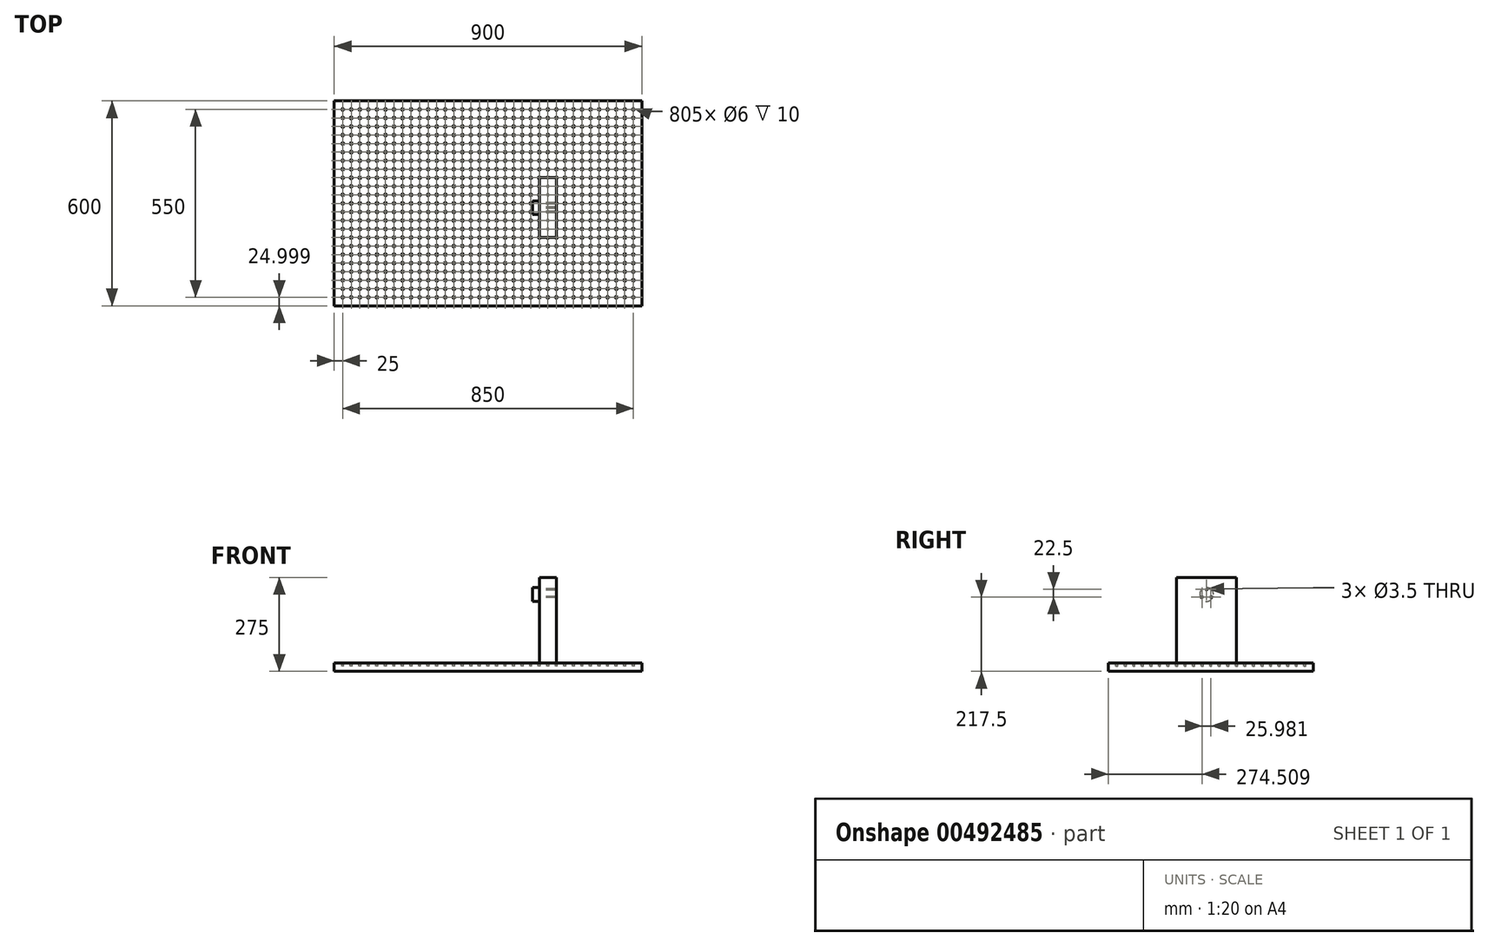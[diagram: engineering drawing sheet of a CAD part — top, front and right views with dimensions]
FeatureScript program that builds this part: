
annotation { "Feature Type Name" : "Feature", "Feature Type Description" : "" }
export const myFeature = defineFeature(function(context is Context, id is Id, definition is map)
    precondition{}
    {
        {
            var Q0;
            Q0=qCreatedBy(makeId("Top.planeOp"),FACE);
            var sketch = newSketch(context, id + "F0", { "sketchPlane" : qUnion([Q0])});
            skLineSegment(sketch, "E0.bottom", {"start": v(0, 7.98) * mm, "end": v(900, 7.98) * mm});
            skLineSegment(sketch, "E0.top", {"start": v(0, 607.98) * mm, "end": v(900, 607.98) * mm});
            skLineSegment(sketch, "E0.left", {"start": v(0, 7.98) * mm, "end": v(0, 607.98) * mm});
            skLineSegment(sketch, "E0.right", {"start": v(900, 7.98) * mm, "end": v(900, 607.98) * mm});
            skSolve(sketch);
        }
        {
            var Q0;
            Q0=makeQuery(id+"F0.imprint","IMPRINT",FACE,{"disambiguationData":[TD([[makeQuery(id+"F0.imprint","IMPRINT",EDGE,{"derivedFrom":sQuery(id+"F0.wireOp",EDGE,"E0.bottom")}),1.0]])]});
            extrude(context, id + "F1", {"entities" : qUnion([Q0]), "depth" : 25 * mm});
        }
        {
            var Q0;
            Q0=makeQuery(id+"F1.opExtrude","CAP_FACE",FACE,{"disambiguationData":[OSD([sQuery(id+"F0.wireOp",EDGE,"E0.bottom"),sQuery(id+"F0.wireOp",EDGE,"E0.top"),sQuery(id+"F0.wireOp",EDGE,"E0.left"),sQuery(id+"F0.wireOp",EDGE,"E0.right")])],"isStart":false});
            var sketch = newSketch(context, id + "F2", { "sketchPlane" : qUnion([Q0])});
            skCircle(sketch, "E1", {"center": v(25, 32.98) * mm, "radius": 3 * mm});
            skCircle(sketch, "E2.0.1.0", {"center": v(25, 57.98) * mm, "radius": 3 * mm});
            skCircle(sketch, "E2.0.2.0", {"center": v(25, 82.98) * mm, "radius": 3 * mm});
            skCircle(sketch, "E2.0.3.0", {"center": v(25, 107.98) * mm, "radius": 3 * mm});
            skCircle(sketch, "E2.0.4.0", {"center": v(25, 132.98) * mm, "radius": 3 * mm});
            skCircle(sketch, "E2.0.5.0", {"center": v(25, 157.98) * mm, "radius": 3 * mm});
            skCircle(sketch, "E2.0.6.0", {"center": v(25, 182.98) * mm, "radius": 3 * mm});
            skCircle(sketch, "E2.0.7.0", {"center": v(25, 207.98) * mm, "radius": 3 * mm});
            skCircle(sketch, "E2.0.8.0", {"center": v(25, 232.98) * mm, "radius": 3 * mm});
            skCircle(sketch, "E2.0.9.0", {"center": v(25, 257.98) * mm, "radius": 3 * mm});
            skCircle(sketch, "E2.0.10.0", {"center": v(25, 282.98) * mm, "radius": 3 * mm});
            skCircle(sketch, "E2.0.11.0", {"center": v(25, 307.98) * mm, "radius": 3 * mm});
            skCircle(sketch, "E2.0.12.0", {"center": v(25, 332.98) * mm, "radius": 3 * mm});
            skCircle(sketch, "E2.0.13.0", {"center": v(25, 357.98) * mm, "radius": 3 * mm});
            skCircle(sketch, "E2.0.14.0", {"center": v(25, 382.98) * mm, "radius": 3 * mm});
            skCircle(sketch, "E2.0.15.0", {"center": v(25, 407.98) * mm, "radius": 3 * mm});
            skCircle(sketch, "E2.0.16.0", {"center": v(25, 432.98) * mm, "radius": 3 * mm});
            skCircle(sketch, "E2.0.17.0", {"center": v(25, 457.98) * mm, "radius": 3 * mm});
            skCircle(sketch, "E2.0.18.0", {"center": v(25, 482.98) * mm, "radius": 3 * mm});
            skCircle(sketch, "E2.0.19.0", {"center": v(25, 507.98) * mm, "radius": 3 * mm});
            skCircle(sketch, "E2.0.20.0", {"center": v(25, 532.98) * mm, "radius": 3 * mm});
            skCircle(sketch, "E2.0.21.0", {"center": v(25, 557.98) * mm, "radius": 3 * mm});
            skCircle(sketch, "E2.0.22.0", {"center": v(25, 582.98) * mm, "radius": 3 * mm});
            skCircle(sketch, "E2.1.0.0", {"center": v(50, 32.98) * mm, "radius": 3 * mm});
            skCircle(sketch, "E2.1.1.0", {"center": v(50, 57.98) * mm, "radius": 3 * mm});
            skCircle(sketch, "E2.1.2.0", {"center": v(50, 82.98) * mm, "radius": 3 * mm});
            skCircle(sketch, "E2.1.3.0", {"center": v(50, 107.98) * mm, "radius": 3 * mm});
            skCircle(sketch, "E2.1.4.0", {"center": v(50, 132.98) * mm, "radius": 3 * mm});
            skCircle(sketch, "E2.1.5.0", {"center": v(50, 157.98) * mm, "radius": 3 * mm});
            skCircle(sketch, "E2.1.6.0", {"center": v(50, 182.98) * mm, "radius": 3 * mm});
            skCircle(sketch, "E2.1.7.0", {"center": v(50, 207.98) * mm, "radius": 3 * mm});
            skCircle(sketch, "E2.1.8.0", {"center": v(50, 232.98) * mm, "radius": 3 * mm});
            skCircle(sketch, "E2.1.9.0", {"center": v(50, 257.98) * mm, "radius": 3 * mm});
            skCircle(sketch, "E2.1.10.0", {"center": v(50, 282.98) * mm, "radius": 3 * mm});
            skCircle(sketch, "E2.1.11.0", {"center": v(50, 307.98) * mm, "radius": 3 * mm});
            skCircle(sketch, "E2.1.12.0", {"center": v(50, 332.98) * mm, "radius": 3 * mm});
            skCircle(sketch, "E2.1.13.0", {"center": v(50, 357.98) * mm, "radius": 3 * mm});
            skCircle(sketch, "E2.1.14.0", {"center": v(50, 382.98) * mm, "radius": 3 * mm});
            skCircle(sketch, "E2.1.15.0", {"center": v(50, 407.98) * mm, "radius": 3 * mm});
            skCircle(sketch, "E2.1.16.0", {"center": v(50, 432.98) * mm, "radius": 3 * mm});
            skCircle(sketch, "E2.1.17.0", {"center": v(50, 457.98) * mm, "radius": 3 * mm});
            skCircle(sketch, "E2.1.18.0", {"center": v(50, 482.98) * mm, "radius": 3 * mm});
            skCircle(sketch, "E2.1.19.0", {"center": v(50, 507.98) * mm, "radius": 3 * mm});
            skCircle(sketch, "E2.1.20.0", {"center": v(50, 532.98) * mm, "radius": 3 * mm});
            skCircle(sketch, "E2.1.21.0", {"center": v(50, 557.98) * mm, "radius": 3 * mm});
            skCircle(sketch, "E2.1.22.0", {"center": v(50, 582.98) * mm, "radius": 3 * mm});
            skCircle(sketch, "E2.2.0.0", {"center": v(75, 32.98) * mm, "radius": 3 * mm});
            skCircle(sketch, "E2.2.1.0", {"center": v(75, 57.98) * mm, "radius": 3 * mm});
            skCircle(sketch, "E2.2.2.0", {"center": v(75, 82.98) * mm, "radius": 3 * mm});
            skCircle(sketch, "E2.2.3.0", {"center": v(75, 107.98) * mm, "radius": 3 * mm});
            skCircle(sketch, "E2.2.4.0", {"center": v(75, 132.98) * mm, "radius": 3 * mm});
            skCircle(sketch, "E2.2.5.0", {"center": v(75, 157.98) * mm, "radius": 3 * mm});
            skCircle(sketch, "E2.2.6.0", {"center": v(75, 182.98) * mm, "radius": 3 * mm});
            skCircle(sketch, "E2.2.7.0", {"center": v(75, 207.98) * mm, "radius": 3 * mm});
            skCircle(sketch, "E2.2.8.0", {"center": v(75, 232.98) * mm, "radius": 3 * mm});
            skCircle(sketch, "E2.2.9.0", {"center": v(75, 257.98) * mm, "radius": 3 * mm});
            skCircle(sketch, "E2.2.10.0", {"center": v(75, 282.98) * mm, "radius": 3 * mm});
            skCircle(sketch, "E2.2.11.0", {"center": v(75, 307.98) * mm, "radius": 3 * mm});
            skCircle(sketch, "E2.2.12.0", {"center": v(75, 332.98) * mm, "radius": 3 * mm});
            skCircle(sketch, "E2.2.13.0", {"center": v(75, 357.98) * mm, "radius": 3 * mm});
            skCircle(sketch, "E2.2.14.0", {"center": v(75, 382.98) * mm, "radius": 3 * mm});
            skCircle(sketch, "E2.2.15.0", {"center": v(75, 407.98) * mm, "radius": 3 * mm});
            skCircle(sketch, "E2.2.16.0", {"center": v(75, 432.98) * mm, "radius": 3 * mm});
            skCircle(sketch, "E2.2.17.0", {"center": v(75, 457.98) * mm, "radius": 3 * mm});
            skCircle(sketch, "E2.2.18.0", {"center": v(75, 482.98) * mm, "radius": 3 * mm});
            skCircle(sketch, "E2.2.19.0", {"center": v(75, 507.98) * mm, "radius": 3 * mm});
            skCircle(sketch, "E2.2.20.0", {"center": v(75, 532.98) * mm, "radius": 3 * mm});
            skCircle(sketch, "E2.2.21.0", {"center": v(75, 557.98) * mm, "radius": 3 * mm});
            skCircle(sketch, "E2.2.22.0", {"center": v(75, 582.98) * mm, "radius": 3 * mm});
            skCircle(sketch, "E2.3.0.0", {"center": v(100, 32.98) * mm, "radius": 3 * mm});
            skCircle(sketch, "E2.3.1.0", {"center": v(100, 57.98) * mm, "radius": 3 * mm});
            skCircle(sketch, "E2.3.2.0", {"center": v(100, 82.98) * mm, "radius": 3 * mm});
            skCircle(sketch, "E2.3.3.0", {"center": v(100, 107.98) * mm, "radius": 3 * mm});
            skCircle(sketch, "E2.3.4.0", {"center": v(100, 132.98) * mm, "radius": 3 * mm});
            skCircle(sketch, "E2.3.5.0", {"center": v(100, 157.98) * mm, "radius": 3 * mm});
            skCircle(sketch, "E2.3.6.0", {"center": v(100, 182.98) * mm, "radius": 3 * mm});
            skCircle(sketch, "E2.3.7.0", {"center": v(100, 207.98) * mm, "radius": 3 * mm});
            skCircle(sketch, "E2.3.8.0", {"center": v(100, 232.98) * mm, "radius": 3 * mm});
            skCircle(sketch, "E2.3.9.0", {"center": v(100, 257.98) * mm, "radius": 3 * mm});
            skCircle(sketch, "E2.3.10.0", {"center": v(100, 282.98) * mm, "radius": 3 * mm});
            skCircle(sketch, "E2.3.11.0", {"center": v(100, 307.98) * mm, "radius": 3 * mm});
            skCircle(sketch, "E2.3.12.0", {"center": v(100, 332.98) * mm, "radius": 3 * mm});
            skCircle(sketch, "E2.3.13.0", {"center": v(100, 357.98) * mm, "radius": 3 * mm});
            skCircle(sketch, "E2.3.14.0", {"center": v(100, 382.98) * mm, "radius": 3 * mm});
            skCircle(sketch, "E2.3.15.0", {"center": v(100, 407.98) * mm, "radius": 3 * mm});
            skCircle(sketch, "E2.3.16.0", {"center": v(100, 432.98) * mm, "radius": 3 * mm});
            skCircle(sketch, "E2.3.17.0", {"center": v(100, 457.98) * mm, "radius": 3 * mm});
            skCircle(sketch, "E2.3.18.0", {"center": v(100, 482.98) * mm, "radius": 3 * mm});
            skCircle(sketch, "E2.3.19.0", {"center": v(100, 507.98) * mm, "radius": 3 * mm});
            skCircle(sketch, "E2.3.20.0", {"center": v(100, 532.98) * mm, "radius": 3 * mm});
            skCircle(sketch, "E2.3.21.0", {"center": v(100, 557.98) * mm, "radius": 3 * mm});
            skCircle(sketch, "E2.3.22.0", {"center": v(100, 582.98) * mm, "radius": 3 * mm});
            skCircle(sketch, "E2.4.0.0", {"center": v(125, 32.98) * mm, "radius": 3 * mm});
            skCircle(sketch, "E2.4.1.0", {"center": v(125, 57.98) * mm, "radius": 3 * mm});
            skCircle(sketch, "E2.4.2.0", {"center": v(125, 82.98) * mm, "radius": 3 * mm});
            skCircle(sketch, "E2.4.3.0", {"center": v(125, 107.98) * mm, "radius": 3 * mm});
            skCircle(sketch, "E2.4.4.0", {"center": v(125, 132.98) * mm, "radius": 3 * mm});
            skCircle(sketch, "E2.4.5.0", {"center": v(125, 157.98) * mm, "radius": 3 * mm});
            skCircle(sketch, "E2.4.6.0", {"center": v(125, 182.98) * mm, "radius": 3 * mm});
            skCircle(sketch, "E2.4.7.0", {"center": v(125, 207.98) * mm, "radius": 3 * mm});
            skCircle(sketch, "E2.4.8.0", {"center": v(125, 232.98) * mm, "radius": 3 * mm});
            skCircle(sketch, "E2.4.9.0", {"center": v(125, 257.98) * mm, "radius": 3 * mm});
            skCircle(sketch, "E2.4.10.0", {"center": v(125, 282.98) * mm, "radius": 3 * mm});
            skCircle(sketch, "E2.4.11.0", {"center": v(125, 307.98) * mm, "radius": 3 * mm});
            skCircle(sketch, "E2.4.12.0", {"center": v(125, 332.98) * mm, "radius": 3 * mm});
            skCircle(sketch, "E2.4.13.0", {"center": v(125, 357.98) * mm, "radius": 3 * mm});
            skCircle(sketch, "E2.4.14.0", {"center": v(125, 382.98) * mm, "radius": 3 * mm});
            skCircle(sketch, "E2.4.15.0", {"center": v(125, 407.98) * mm, "radius": 3 * mm});
            skCircle(sketch, "E2.4.16.0", {"center": v(125, 432.98) * mm, "radius": 3 * mm});
            skCircle(sketch, "E2.4.17.0", {"center": v(125, 457.98) * mm, "radius": 3 * mm});
            skCircle(sketch, "E2.4.18.0", {"center": v(125, 482.98) * mm, "radius": 3 * mm});
            skCircle(sketch, "E2.4.19.0", {"center": v(125, 507.98) * mm, "radius": 3 * mm});
            skCircle(sketch, "E2.4.20.0", {"center": v(125, 532.98) * mm, "radius": 3 * mm});
            skCircle(sketch, "E2.4.21.0", {"center": v(125, 557.98) * mm, "radius": 3 * mm});
            skCircle(sketch, "E2.4.22.0", {"center": v(125, 582.98) * mm, "radius": 3 * mm});
            skCircle(sketch, "E2.5.0.0", {"center": v(150, 32.98) * mm, "radius": 3 * mm});
            skCircle(sketch, "E2.5.1.0", {"center": v(150, 57.98) * mm, "radius": 3 * mm});
            skCircle(sketch, "E2.5.2.0", {"center": v(150, 82.98) * mm, "radius": 3 * mm});
            skCircle(sketch, "E2.5.3.0", {"center": v(150, 107.98) * mm, "radius": 3 * mm});
            skCircle(sketch, "E2.5.4.0", {"center": v(150, 132.98) * mm, "radius": 3 * mm});
            skCircle(sketch, "E2.5.5.0", {"center": v(150, 157.98) * mm, "radius": 3 * mm});
            skCircle(sketch, "E2.5.6.0", {"center": v(150, 182.98) * mm, "radius": 3 * mm});
            skCircle(sketch, "E2.5.7.0", {"center": v(150, 207.98) * mm, "radius": 3 * mm});
            skCircle(sketch, "E2.5.8.0", {"center": v(150, 232.98) * mm, "radius": 3 * mm});
            skCircle(sketch, "E2.5.9.0", {"center": v(150, 257.98) * mm, "radius": 3 * mm});
            skCircle(sketch, "E2.5.10.0", {"center": v(150, 282.98) * mm, "radius": 3 * mm});
            skCircle(sketch, "E2.5.11.0", {"center": v(150, 307.98) * mm, "radius": 3 * mm});
            skCircle(sketch, "E2.5.12.0", {"center": v(150, 332.98) * mm, "radius": 3 * mm});
            skCircle(sketch, "E2.5.13.0", {"center": v(150, 357.98) * mm, "radius": 3 * mm});
            skCircle(sketch, "E2.5.14.0", {"center": v(150, 382.98) * mm, "radius": 3 * mm});
            skCircle(sketch, "E2.5.15.0", {"center": v(150, 407.98) * mm, "radius": 3 * mm});
            skCircle(sketch, "E2.5.16.0", {"center": v(150, 432.98) * mm, "radius": 3 * mm});
            skCircle(sketch, "E2.5.17.0", {"center": v(150, 457.98) * mm, "radius": 3 * mm});
            skCircle(sketch, "E2.5.18.0", {"center": v(150, 482.98) * mm, "radius": 3 * mm});
            skCircle(sketch, "E2.5.19.0", {"center": v(150, 507.98) * mm, "radius": 3 * mm});
            skCircle(sketch, "E2.5.20.0", {"center": v(150, 532.98) * mm, "radius": 3 * mm});
            skCircle(sketch, "E2.5.21.0", {"center": v(150, 557.98) * mm, "radius": 3 * mm});
            skCircle(sketch, "E2.5.22.0", {"center": v(150, 582.98) * mm, "radius": 3 * mm});
            skCircle(sketch, "E2.6.0.0", {"center": v(175, 32.98) * mm, "radius": 3 * mm});
            skCircle(sketch, "E2.6.1.0", {"center": v(175, 57.98) * mm, "radius": 3 * mm});
            skCircle(sketch, "E2.6.2.0", {"center": v(175, 82.98) * mm, "radius": 3 * mm});
            skCircle(sketch, "E2.6.3.0", {"center": v(175, 107.98) * mm, "radius": 3 * mm});
            skCircle(sketch, "E2.6.4.0", {"center": v(175, 132.98) * mm, "radius": 3 * mm});
            skCircle(sketch, "E2.6.5.0", {"center": v(175, 157.98) * mm, "radius": 3 * mm});
            skCircle(sketch, "E2.6.6.0", {"center": v(175, 182.98) * mm, "radius": 3 * mm});
            skCircle(sketch, "E2.6.7.0", {"center": v(175, 207.98) * mm, "radius": 3 * mm});
            skCircle(sketch, "E2.6.8.0", {"center": v(175, 232.98) * mm, "radius": 3 * mm});
            skCircle(sketch, "E2.6.9.0", {"center": v(175, 257.98) * mm, "radius": 3 * mm});
            skCircle(sketch, "E2.6.10.0", {"center": v(175, 282.98) * mm, "radius": 3 * mm});
            skCircle(sketch, "E2.6.11.0", {"center": v(175, 307.98) * mm, "radius": 3 * mm});
            skCircle(sketch, "E2.6.12.0", {"center": v(175, 332.98) * mm, "radius": 3 * mm});
            skCircle(sketch, "E2.6.13.0", {"center": v(175, 357.98) * mm, "radius": 3 * mm});
            skCircle(sketch, "E2.6.14.0", {"center": v(175, 382.98) * mm, "radius": 3 * mm});
            skCircle(sketch, "E2.6.15.0", {"center": v(175, 407.98) * mm, "radius": 3 * mm});
            skCircle(sketch, "E2.6.16.0", {"center": v(175, 432.98) * mm, "radius": 3 * mm});
            skCircle(sketch, "E2.6.17.0", {"center": v(175, 457.98) * mm, "radius": 3 * mm});
            skCircle(sketch, "E2.6.18.0", {"center": v(175, 482.98) * mm, "radius": 3 * mm});
            skCircle(sketch, "E2.6.19.0", {"center": v(175, 507.98) * mm, "radius": 3 * mm});
            skCircle(sketch, "E2.6.20.0", {"center": v(175, 532.98) * mm, "radius": 3 * mm});
            skCircle(sketch, "E2.6.21.0", {"center": v(175, 557.98) * mm, "radius": 3 * mm});
            skCircle(sketch, "E2.6.22.0", {"center": v(175, 582.98) * mm, "radius": 3 * mm});
            skCircle(sketch, "E2.7.0.0", {"center": v(200, 32.98) * mm, "radius": 3 * mm});
            skCircle(sketch, "E2.7.1.0", {"center": v(200, 57.98) * mm, "radius": 3 * mm});
            skCircle(sketch, "E2.7.2.0", {"center": v(200, 82.98) * mm, "radius": 3 * mm});
            skCircle(sketch, "E2.7.3.0", {"center": v(200, 107.98) * mm, "radius": 3 * mm});
            skCircle(sketch, "E2.7.4.0", {"center": v(200, 132.98) * mm, "radius": 3 * mm});
            skCircle(sketch, "E2.7.5.0", {"center": v(200, 157.98) * mm, "radius": 3 * mm});
            skCircle(sketch, "E2.7.6.0", {"center": v(200, 182.98) * mm, "radius": 3 * mm});
            skCircle(sketch, "E2.7.7.0", {"center": v(200, 207.98) * mm, "radius": 3 * mm});
            skCircle(sketch, "E2.7.8.0", {"center": v(200, 232.98) * mm, "radius": 3 * mm});
            skCircle(sketch, "E2.7.9.0", {"center": v(200, 257.98) * mm, "radius": 3 * mm});
            skCircle(sketch, "E2.7.10.0", {"center": v(200, 282.98) * mm, "radius": 3 * mm});
            skCircle(sketch, "E2.7.11.0", {"center": v(200, 307.98) * mm, "radius": 3 * mm});
            skCircle(sketch, "E2.7.12.0", {"center": v(200, 332.98) * mm, "radius": 3 * mm});
            skCircle(sketch, "E2.7.13.0", {"center": v(200, 357.98) * mm, "radius": 3 * mm});
            skCircle(sketch, "E2.7.14.0", {"center": v(200, 382.98) * mm, "radius": 3 * mm});
            skCircle(sketch, "E2.7.15.0", {"center": v(200, 407.98) * mm, "radius": 3 * mm});
            skCircle(sketch, "E2.7.16.0", {"center": v(200, 432.98) * mm, "radius": 3 * mm});
            skCircle(sketch, "E2.7.17.0", {"center": v(200, 457.98) * mm, "radius": 3 * mm});
            skCircle(sketch, "E2.7.18.0", {"center": v(200, 482.98) * mm, "radius": 3 * mm});
            skCircle(sketch, "E2.7.19.0", {"center": v(200, 507.98) * mm, "radius": 3 * mm});
            skCircle(sketch, "E2.7.20.0", {"center": v(200, 532.98) * mm, "radius": 3 * mm});
            skCircle(sketch, "E2.7.21.0", {"center": v(200, 557.98) * mm, "radius": 3 * mm});
            skCircle(sketch, "E2.7.22.0", {"center": v(200, 582.98) * mm, "radius": 3 * mm});
            skCircle(sketch, "E2.8.0.0", {"center": v(225, 32.98) * mm, "radius": 3 * mm});
            skCircle(sketch, "E2.8.1.0", {"center": v(225, 57.98) * mm, "radius": 3 * mm});
            skCircle(sketch, "E2.8.2.0", {"center": v(225, 82.98) * mm, "radius": 3 * mm});
            skCircle(sketch, "E2.8.3.0", {"center": v(225, 107.98) * mm, "radius": 3 * mm});
            skCircle(sketch, "E2.8.4.0", {"center": v(225, 132.98) * mm, "radius": 3 * mm});
            skCircle(sketch, "E2.8.5.0", {"center": v(225, 157.98) * mm, "radius": 3 * mm});
            skCircle(sketch, "E2.8.6.0", {"center": v(225, 182.98) * mm, "radius": 3 * mm});
            skCircle(sketch, "E2.8.7.0", {"center": v(225, 207.98) * mm, "radius": 3 * mm});
            skCircle(sketch, "E2.8.8.0", {"center": v(225, 232.98) * mm, "radius": 3 * mm});
            skCircle(sketch, "E2.8.9.0", {"center": v(225, 257.98) * mm, "radius": 3 * mm});
            skCircle(sketch, "E2.8.10.0", {"center": v(225, 282.98) * mm, "radius": 3 * mm});
            skCircle(sketch, "E2.8.11.0", {"center": v(225, 307.98) * mm, "radius": 3 * mm});
            skCircle(sketch, "E2.8.12.0", {"center": v(225, 332.98) * mm, "radius": 3 * mm});
            skCircle(sketch, "E2.8.13.0", {"center": v(225, 357.98) * mm, "radius": 3 * mm});
            skCircle(sketch, "E2.8.14.0", {"center": v(225, 382.98) * mm, "radius": 3 * mm});
            skCircle(sketch, "E2.8.15.0", {"center": v(225, 407.98) * mm, "radius": 3 * mm});
            skCircle(sketch, "E2.8.16.0", {"center": v(225, 432.98) * mm, "radius": 3 * mm});
            skCircle(sketch, "E2.8.17.0", {"center": v(225, 457.98) * mm, "radius": 3 * mm});
            skCircle(sketch, "E2.8.18.0", {"center": v(225, 482.98) * mm, "radius": 3 * mm});
            skCircle(sketch, "E2.8.19.0", {"center": v(225, 507.98) * mm, "radius": 3 * mm});
            skCircle(sketch, "E2.8.20.0", {"center": v(225, 532.98) * mm, "radius": 3 * mm});
            skCircle(sketch, "E2.8.21.0", {"center": v(225, 557.98) * mm, "radius": 3 * mm});
            skCircle(sketch, "E2.8.22.0", {"center": v(225, 582.98) * mm, "radius": 3 * mm});
            skCircle(sketch, "E2.9.0.0", {"center": v(250, 32.98) * mm, "radius": 3 * mm});
            skCircle(sketch, "E2.9.1.0", {"center": v(250, 57.98) * mm, "radius": 3 * mm});
            skCircle(sketch, "E2.9.2.0", {"center": v(250, 82.98) * mm, "radius": 3 * mm});
            skCircle(sketch, "E2.9.3.0", {"center": v(250, 107.98) * mm, "radius": 3 * mm});
            skCircle(sketch, "E2.9.4.0", {"center": v(250, 132.98) * mm, "radius": 3 * mm});
            skCircle(sketch, "E2.9.5.0", {"center": v(250, 157.98) * mm, "radius": 3 * mm});
            skCircle(sketch, "E2.9.6.0", {"center": v(250, 182.98) * mm, "radius": 3 * mm});
            skCircle(sketch, "E2.9.7.0", {"center": v(250, 207.98) * mm, "radius": 3 * mm});
            skCircle(sketch, "E2.9.8.0", {"center": v(250, 232.98) * mm, "radius": 3 * mm});
            skCircle(sketch, "E2.9.9.0", {"center": v(250, 257.98) * mm, "radius": 3 * mm});
            skCircle(sketch, "E2.9.10.0", {"center": v(250, 282.98) * mm, "radius": 3 * mm});
            skCircle(sketch, "E2.9.11.0", {"center": v(250, 307.98) * mm, "radius": 3 * mm});
            skCircle(sketch, "E2.9.12.0", {"center": v(250, 332.98) * mm, "radius": 3 * mm});
            skCircle(sketch, "E2.9.13.0", {"center": v(250, 357.98) * mm, "radius": 3 * mm});
            skCircle(sketch, "E2.9.14.0", {"center": v(250, 382.98) * mm, "radius": 3 * mm});
            skCircle(sketch, "E2.9.15.0", {"center": v(250, 407.98) * mm, "radius": 3 * mm});
            skCircle(sketch, "E2.9.16.0", {"center": v(250, 432.98) * mm, "radius": 3 * mm});
            skCircle(sketch, "E2.9.17.0", {"center": v(250, 457.98) * mm, "radius": 3 * mm});
            skCircle(sketch, "E2.9.18.0", {"center": v(250, 482.98) * mm, "radius": 3 * mm});
            skCircle(sketch, "E2.9.19.0", {"center": v(250, 507.98) * mm, "radius": 3 * mm});
            skCircle(sketch, "E2.9.20.0", {"center": v(250, 532.98) * mm, "radius": 3 * mm});
            skCircle(sketch, "E2.9.21.0", {"center": v(250, 557.98) * mm, "radius": 3 * mm});
            skCircle(sketch, "E2.9.22.0", {"center": v(250, 582.98) * mm, "radius": 3 * mm});
            skCircle(sketch, "E2.10.0.0", {"center": v(275, 32.98) * mm, "radius": 3 * mm});
            skCircle(sketch, "E2.10.1.0", {"center": v(275, 57.98) * mm, "radius": 3 * mm});
            skCircle(sketch, "E2.10.2.0", {"center": v(275, 82.98) * mm, "radius": 3 * mm});
            skCircle(sketch, "E2.10.3.0", {"center": v(275, 107.98) * mm, "radius": 3 * mm});
            skCircle(sketch, "E2.10.4.0", {"center": v(275, 132.98) * mm, "radius": 3 * mm});
            skCircle(sketch, "E2.10.5.0", {"center": v(275, 157.98) * mm, "radius": 3 * mm});
            skCircle(sketch, "E2.10.6.0", {"center": v(275, 182.98) * mm, "radius": 3 * mm});
            skCircle(sketch, "E2.10.7.0", {"center": v(275, 207.98) * mm, "radius": 3 * mm});
            skCircle(sketch, "E2.10.8.0", {"center": v(275, 232.98) * mm, "radius": 3 * mm});
            skCircle(sketch, "E2.10.9.0", {"center": v(275, 257.98) * mm, "radius": 3 * mm});
            skCircle(sketch, "E2.10.10.0", {"center": v(275, 282.98) * mm, "radius": 3 * mm});
            skCircle(sketch, "E2.10.11.0", {"center": v(275, 307.98) * mm, "radius": 3 * mm});
            skCircle(sketch, "E2.10.12.0", {"center": v(275, 332.98) * mm, "radius": 3 * mm});
            skCircle(sketch, "E2.10.13.0", {"center": v(275, 357.98) * mm, "radius": 3 * mm});
            skCircle(sketch, "E2.10.14.0", {"center": v(275, 382.98) * mm, "radius": 3 * mm});
            skCircle(sketch, "E2.10.15.0", {"center": v(275, 407.98) * mm, "radius": 3 * mm});
            skCircle(sketch, "E2.10.16.0", {"center": v(275, 432.98) * mm, "radius": 3 * mm});
            skCircle(sketch, "E2.10.17.0", {"center": v(275, 457.98) * mm, "radius": 3 * mm});
            skCircle(sketch, "E2.10.18.0", {"center": v(275, 482.98) * mm, "radius": 3 * mm});
            skCircle(sketch, "E2.10.19.0", {"center": v(275, 507.98) * mm, "radius": 3 * mm});
            skCircle(sketch, "E2.10.20.0", {"center": v(275, 532.98) * mm, "radius": 3 * mm});
            skCircle(sketch, "E2.10.21.0", {"center": v(275, 557.98) * mm, "radius": 3 * mm});
            skCircle(sketch, "E2.10.22.0", {"center": v(275, 582.98) * mm, "radius": 3 * mm});
            skCircle(sketch, "E2.11.0.0", {"center": v(300, 32.98) * mm, "radius": 3 * mm});
            skCircle(sketch, "E2.11.1.0", {"center": v(300, 57.98) * mm, "radius": 3 * mm});
            skCircle(sketch, "E2.11.2.0", {"center": v(300, 82.98) * mm, "radius": 3 * mm});
            skCircle(sketch, "E2.11.3.0", {"center": v(300, 107.98) * mm, "radius": 3 * mm});
            skCircle(sketch, "E2.11.4.0", {"center": v(300, 132.98) * mm, "radius": 3 * mm});
            skCircle(sketch, "E2.11.5.0", {"center": v(300, 157.98) * mm, "radius": 3 * mm});
            skCircle(sketch, "E2.11.6.0", {"center": v(300, 182.98) * mm, "radius": 3 * mm});
            skCircle(sketch, "E2.11.7.0", {"center": v(300, 207.98) * mm, "radius": 3 * mm});
            skCircle(sketch, "E2.11.8.0", {"center": v(300, 232.98) * mm, "radius": 3 * mm});
            skCircle(sketch, "E2.11.9.0", {"center": v(300, 257.98) * mm, "radius": 3 * mm});
            skCircle(sketch, "E2.11.10.0", {"center": v(300, 282.98) * mm, "radius": 3 * mm});
            skCircle(sketch, "E2.11.11.0", {"center": v(300, 307.98) * mm, "radius": 3 * mm});
            skCircle(sketch, "E2.11.12.0", {"center": v(300, 332.98) * mm, "radius": 3 * mm});
            skCircle(sketch, "E2.11.13.0", {"center": v(300, 357.98) * mm, "radius": 3 * mm});
            skCircle(sketch, "E2.11.14.0", {"center": v(300, 382.98) * mm, "radius": 3 * mm});
            skCircle(sketch, "E2.11.15.0", {"center": v(300, 407.98) * mm, "radius": 3 * mm});
            skCircle(sketch, "E2.11.16.0", {"center": v(300, 432.98) * mm, "radius": 3 * mm});
            skCircle(sketch, "E2.11.17.0", {"center": v(300, 457.98) * mm, "radius": 3 * mm});
            skCircle(sketch, "E2.11.18.0", {"center": v(300, 482.98) * mm, "radius": 3 * mm});
            skCircle(sketch, "E2.11.19.0", {"center": v(300, 507.98) * mm, "radius": 3 * mm});
            skCircle(sketch, "E2.11.20.0", {"center": v(300, 532.98) * mm, "radius": 3 * mm});
            skCircle(sketch, "E2.11.21.0", {"center": v(300, 557.98) * mm, "radius": 3 * mm});
            skCircle(sketch, "E2.11.22.0", {"center": v(300, 582.98) * mm, "radius": 3 * mm});
            skCircle(sketch, "E2.12.0.0", {"center": v(325, 32.98) * mm, "radius": 3 * mm});
            skCircle(sketch, "E2.12.1.0", {"center": v(325, 57.98) * mm, "radius": 3 * mm});
            skCircle(sketch, "E2.12.2.0", {"center": v(325, 82.98) * mm, "radius": 3 * mm});
            skCircle(sketch, "E2.12.3.0", {"center": v(325, 107.98) * mm, "radius": 3 * mm});
            skCircle(sketch, "E2.12.4.0", {"center": v(325, 132.98) * mm, "radius": 3 * mm});
            skCircle(sketch, "E2.12.5.0", {"center": v(325, 157.98) * mm, "radius": 3 * mm});
            skCircle(sketch, "E2.12.6.0", {"center": v(325, 182.98) * mm, "radius": 3 * mm});
            skCircle(sketch, "E2.12.7.0", {"center": v(325, 207.98) * mm, "radius": 3 * mm});
            skCircle(sketch, "E2.12.8.0", {"center": v(325, 232.98) * mm, "radius": 3 * mm});
            skCircle(sketch, "E2.12.9.0", {"center": v(325, 257.98) * mm, "radius": 3 * mm});
            skCircle(sketch, "E2.12.10.0", {"center": v(325, 282.98) * mm, "radius": 3 * mm});
            skCircle(sketch, "E2.12.11.0", {"center": v(325, 307.98) * mm, "radius": 3 * mm});
            skCircle(sketch, "E2.12.12.0", {"center": v(325, 332.98) * mm, "radius": 3 * mm});
            skCircle(sketch, "E2.12.13.0", {"center": v(325, 357.98) * mm, "radius": 3 * mm});
            skCircle(sketch, "E2.12.14.0", {"center": v(325, 382.98) * mm, "radius": 3 * mm});
            skCircle(sketch, "E2.12.15.0", {"center": v(325, 407.98) * mm, "radius": 3 * mm});
            skCircle(sketch, "E2.12.16.0", {"center": v(325, 432.98) * mm, "radius": 3 * mm});
            skCircle(sketch, "E2.12.17.0", {"center": v(325, 457.98) * mm, "radius": 3 * mm});
            skCircle(sketch, "E2.12.18.0", {"center": v(325, 482.98) * mm, "radius": 3 * mm});
            skCircle(sketch, "E2.12.19.0", {"center": v(325, 507.98) * mm, "radius": 3 * mm});
            skCircle(sketch, "E2.12.20.0", {"center": v(325, 532.98) * mm, "radius": 3 * mm});
            skCircle(sketch, "E2.12.21.0", {"center": v(325, 557.98) * mm, "radius": 3 * mm});
            skCircle(sketch, "E2.12.22.0", {"center": v(325, 582.98) * mm, "radius": 3 * mm});
            skCircle(sketch, "E2.13.0.0", {"center": v(350, 32.98) * mm, "radius": 3 * mm});
            skCircle(sketch, "E2.13.1.0", {"center": v(350, 57.98) * mm, "radius": 3 * mm});
            skCircle(sketch, "E2.13.2.0", {"center": v(350, 82.98) * mm, "radius": 3 * mm});
            skCircle(sketch, "E2.13.3.0", {"center": v(350, 107.98) * mm, "radius": 3 * mm});
            skCircle(sketch, "E2.13.4.0", {"center": v(350, 132.98) * mm, "radius": 3 * mm});
            skCircle(sketch, "E2.13.5.0", {"center": v(350, 157.98) * mm, "radius": 3 * mm});
            skCircle(sketch, "E2.13.6.0", {"center": v(350, 182.98) * mm, "radius": 3 * mm});
            skCircle(sketch, "E2.13.7.0", {"center": v(350, 207.98) * mm, "radius": 3 * mm});
            skCircle(sketch, "E2.13.8.0", {"center": v(350, 232.98) * mm, "radius": 3 * mm});
            skCircle(sketch, "E2.13.9.0", {"center": v(350, 257.98) * mm, "radius": 3 * mm});
            skCircle(sketch, "E2.13.10.0", {"center": v(350, 282.98) * mm, "radius": 3 * mm});
            skCircle(sketch, "E2.13.11.0", {"center": v(350, 307.98) * mm, "radius": 3 * mm});
            skCircle(sketch, "E2.13.12.0", {"center": v(350, 332.98) * mm, "radius": 3 * mm});
            skCircle(sketch, "E2.13.13.0", {"center": v(350, 357.98) * mm, "radius": 3 * mm});
            skCircle(sketch, "E2.13.14.0", {"center": v(350, 382.98) * mm, "radius": 3 * mm});
            skCircle(sketch, "E2.13.15.0", {"center": v(350, 407.98) * mm, "radius": 3 * mm});
            skCircle(sketch, "E2.13.16.0", {"center": v(350, 432.98) * mm, "radius": 3 * mm});
            skCircle(sketch, "E2.13.17.0", {"center": v(350, 457.98) * mm, "radius": 3 * mm});
            skCircle(sketch, "E2.13.18.0", {"center": v(350, 482.98) * mm, "radius": 3 * mm});
            skCircle(sketch, "E2.13.19.0", {"center": v(350, 507.98) * mm, "radius": 3 * mm});
            skCircle(sketch, "E2.13.20.0", {"center": v(350, 532.98) * mm, "radius": 3 * mm});
            skCircle(sketch, "E2.13.21.0", {"center": v(350, 557.98) * mm, "radius": 3 * mm});
            skCircle(sketch, "E2.13.22.0", {"center": v(350, 582.98) * mm, "radius": 3 * mm});
            skCircle(sketch, "E2.14.0.0", {"center": v(375, 32.98) * mm, "radius": 3 * mm});
            skCircle(sketch, "E2.14.1.0", {"center": v(375, 57.98) * mm, "radius": 3 * mm});
            skCircle(sketch, "E2.14.2.0", {"center": v(375, 82.98) * mm, "radius": 3 * mm});
            skCircle(sketch, "E2.14.3.0", {"center": v(375, 107.98) * mm, "radius": 3 * mm});
            skCircle(sketch, "E2.14.4.0", {"center": v(375, 132.98) * mm, "radius": 3 * mm});
            skCircle(sketch, "E2.14.5.0", {"center": v(375, 157.98) * mm, "radius": 3 * mm});
            skCircle(sketch, "E2.14.6.0", {"center": v(375, 182.98) * mm, "radius": 3 * mm});
            skCircle(sketch, "E2.14.7.0", {"center": v(375, 207.98) * mm, "radius": 3 * mm});
            skCircle(sketch, "E2.14.8.0", {"center": v(375, 232.98) * mm, "radius": 3 * mm});
            skCircle(sketch, "E2.14.9.0", {"center": v(375, 257.98) * mm, "radius": 3 * mm});
            skCircle(sketch, "E2.14.10.0", {"center": v(375, 282.98) * mm, "radius": 3 * mm});
            skCircle(sketch, "E2.14.11.0", {"center": v(375, 307.98) * mm, "radius": 3 * mm});
            skCircle(sketch, "E2.14.12.0", {"center": v(375, 332.98) * mm, "radius": 3 * mm});
            skCircle(sketch, "E2.14.13.0", {"center": v(375, 357.98) * mm, "radius": 3 * mm});
            skCircle(sketch, "E2.14.14.0", {"center": v(375, 382.98) * mm, "radius": 3 * mm});
            skCircle(sketch, "E2.14.15.0", {"center": v(375, 407.98) * mm, "radius": 3 * mm});
            skCircle(sketch, "E2.14.16.0", {"center": v(375, 432.98) * mm, "radius": 3 * mm});
            skCircle(sketch, "E2.14.17.0", {"center": v(375, 457.98) * mm, "radius": 3 * mm});
            skCircle(sketch, "E2.14.18.0", {"center": v(375, 482.98) * mm, "radius": 3 * mm});
            skCircle(sketch, "E2.14.19.0", {"center": v(375, 507.98) * mm, "radius": 3 * mm});
            skCircle(sketch, "E2.14.20.0", {"center": v(375, 532.98) * mm, "radius": 3 * mm});
            skCircle(sketch, "E2.14.21.0", {"center": v(375, 557.98) * mm, "radius": 3 * mm});
            skCircle(sketch, "E2.14.22.0", {"center": v(375, 582.98) * mm, "radius": 3 * mm});
            skCircle(sketch, "E2.15.0.0", {"center": v(400, 32.98) * mm, "radius": 3 * mm});
            skCircle(sketch, "E2.15.1.0", {"center": v(400, 57.98) * mm, "radius": 3 * mm});
            skCircle(sketch, "E2.15.2.0", {"center": v(400, 82.98) * mm, "radius": 3 * mm});
            skCircle(sketch, "E2.15.3.0", {"center": v(400, 107.98) * mm, "radius": 3 * mm});
            skCircle(sketch, "E2.15.4.0", {"center": v(400, 132.98) * mm, "radius": 3 * mm});
            skCircle(sketch, "E2.15.5.0", {"center": v(400, 157.98) * mm, "radius": 3 * mm});
            skCircle(sketch, "E2.15.6.0", {"center": v(400, 182.98) * mm, "radius": 3 * mm});
            skCircle(sketch, "E2.15.7.0", {"center": v(400, 207.98) * mm, "radius": 3 * mm});
            skCircle(sketch, "E2.15.8.0", {"center": v(400, 232.98) * mm, "radius": 3 * mm});
            skCircle(sketch, "E2.15.9.0", {"center": v(400, 257.98) * mm, "radius": 3 * mm});
            skCircle(sketch, "E2.15.10.0", {"center": v(400, 282.98) * mm, "radius": 3 * mm});
            skCircle(sketch, "E2.15.11.0", {"center": v(400, 307.98) * mm, "radius": 3 * mm});
            skCircle(sketch, "E2.15.12.0", {"center": v(400, 332.98) * mm, "radius": 3 * mm});
            skCircle(sketch, "E2.15.13.0", {"center": v(400, 357.98) * mm, "radius": 3 * mm});
            skCircle(sketch, "E2.15.14.0", {"center": v(400, 382.98) * mm, "radius": 3 * mm});
            skCircle(sketch, "E2.15.15.0", {"center": v(400, 407.98) * mm, "radius": 3 * mm});
            skCircle(sketch, "E2.15.16.0", {"center": v(400, 432.98) * mm, "radius": 3 * mm});
            skCircle(sketch, "E2.15.17.0", {"center": v(400, 457.98) * mm, "radius": 3 * mm});
            skCircle(sketch, "E2.15.18.0", {"center": v(400, 482.98) * mm, "radius": 3 * mm});
            skCircle(sketch, "E2.15.19.0", {"center": v(400, 507.98) * mm, "radius": 3 * mm});
            skCircle(sketch, "E2.15.20.0", {"center": v(400, 532.98) * mm, "radius": 3 * mm});
            skCircle(sketch, "E2.15.21.0", {"center": v(400, 557.98) * mm, "radius": 3 * mm});
            skCircle(sketch, "E2.15.22.0", {"center": v(400, 582.98) * mm, "radius": 3 * mm});
            skCircle(sketch, "E2.16.0.0", {"center": v(425, 32.98) * mm, "radius": 3 * mm});
            skCircle(sketch, "E2.16.1.0", {"center": v(425, 57.98) * mm, "radius": 3 * mm});
            skCircle(sketch, "E2.16.2.0", {"center": v(425, 82.98) * mm, "radius": 3 * mm});
            skCircle(sketch, "E2.16.3.0", {"center": v(425, 107.98) * mm, "radius": 3 * mm});
            skCircle(sketch, "E2.16.4.0", {"center": v(425, 132.98) * mm, "radius": 3 * mm});
            skCircle(sketch, "E2.16.5.0", {"center": v(425, 157.98) * mm, "radius": 3 * mm});
            skCircle(sketch, "E2.16.6.0", {"center": v(425, 182.98) * mm, "radius": 3 * mm});
            skCircle(sketch, "E2.16.7.0", {"center": v(425, 207.98) * mm, "radius": 3 * mm});
            skCircle(sketch, "E2.16.8.0", {"center": v(425, 232.98) * mm, "radius": 3 * mm});
            skCircle(sketch, "E2.16.9.0", {"center": v(425, 257.98) * mm, "radius": 3 * mm});
            skCircle(sketch, "E2.16.10.0", {"center": v(425, 282.98) * mm, "radius": 3 * mm});
            skCircle(sketch, "E2.16.11.0", {"center": v(425, 307.98) * mm, "radius": 3 * mm});
            skCircle(sketch, "E2.16.12.0", {"center": v(425, 332.98) * mm, "radius": 3 * mm});
            skCircle(sketch, "E2.16.13.0", {"center": v(425, 357.98) * mm, "radius": 3 * mm});
            skCircle(sketch, "E2.16.14.0", {"center": v(425, 382.98) * mm, "radius": 3 * mm});
            skCircle(sketch, "E2.16.15.0", {"center": v(425, 407.98) * mm, "radius": 3 * mm});
            skCircle(sketch, "E2.16.16.0", {"center": v(425, 432.98) * mm, "radius": 3 * mm});
            skCircle(sketch, "E2.16.17.0", {"center": v(425, 457.98) * mm, "radius": 3 * mm});
            skCircle(sketch, "E2.16.18.0", {"center": v(425, 482.98) * mm, "radius": 3 * mm});
            skCircle(sketch, "E2.16.19.0", {"center": v(425, 507.98) * mm, "radius": 3 * mm});
            skCircle(sketch, "E2.16.20.0", {"center": v(425, 532.98) * mm, "radius": 3 * mm});
            skCircle(sketch, "E2.16.21.0", {"center": v(425, 557.98) * mm, "radius": 3 * mm});
            skCircle(sketch, "E2.16.22.0", {"center": v(425, 582.98) * mm, "radius": 3 * mm});
            skCircle(sketch, "E2.17.0.0", {"center": v(450, 32.98) * mm, "radius": 3 * mm});
            skCircle(sketch, "E2.17.1.0", {"center": v(450, 57.98) * mm, "radius": 3 * mm});
            skCircle(sketch, "E2.17.2.0", {"center": v(450, 82.98) * mm, "radius": 3 * mm});
            skCircle(sketch, "E2.17.3.0", {"center": v(450, 107.98) * mm, "radius": 3 * mm});
            skCircle(sketch, "E2.17.4.0", {"center": v(450, 132.98) * mm, "radius": 3 * mm});
            skCircle(sketch, "E2.17.5.0", {"center": v(450, 157.98) * mm, "radius": 3 * mm});
            skCircle(sketch, "E2.17.6.0", {"center": v(450, 182.98) * mm, "radius": 3 * mm});
            skCircle(sketch, "E2.17.7.0", {"center": v(450, 207.98) * mm, "radius": 3 * mm});
            skCircle(sketch, "E2.17.8.0", {"center": v(450, 232.98) * mm, "radius": 3 * mm});
            skCircle(sketch, "E2.17.9.0", {"center": v(450, 257.98) * mm, "radius": 3 * mm});
            skCircle(sketch, "E2.17.10.0", {"center": v(450, 282.98) * mm, "radius": 3 * mm});
            skCircle(sketch, "E2.17.11.0", {"center": v(450, 307.98) * mm, "radius": 3 * mm});
            skCircle(sketch, "E2.17.12.0", {"center": v(450, 332.98) * mm, "radius": 3 * mm});
            skCircle(sketch, "E2.17.13.0", {"center": v(450, 357.98) * mm, "radius": 3 * mm});
            skCircle(sketch, "E2.17.14.0", {"center": v(450, 382.98) * mm, "radius": 3 * mm});
            skCircle(sketch, "E2.17.15.0", {"center": v(450, 407.98) * mm, "radius": 3 * mm});
            skCircle(sketch, "E2.17.16.0", {"center": v(450, 432.98) * mm, "radius": 3 * mm});
            skCircle(sketch, "E2.17.17.0", {"center": v(450, 457.98) * mm, "radius": 3 * mm});
            skCircle(sketch, "E2.17.18.0", {"center": v(450, 482.98) * mm, "radius": 3 * mm});
            skCircle(sketch, "E2.17.19.0", {"center": v(450, 507.98) * mm, "radius": 3 * mm});
            skCircle(sketch, "E2.17.20.0", {"center": v(450, 532.98) * mm, "radius": 3 * mm});
            skCircle(sketch, "E2.17.21.0", {"center": v(450, 557.98) * mm, "radius": 3 * mm});
            skCircle(sketch, "E2.17.22.0", {"center": v(450, 582.98) * mm, "radius": 3 * mm});
            skCircle(sketch, "E2.18.0.0", {"center": v(475, 32.98) * mm, "radius": 3 * mm});
            skCircle(sketch, "E2.18.1.0", {"center": v(475, 57.98) * mm, "radius": 3 * mm});
            skCircle(sketch, "E2.18.2.0", {"center": v(475, 82.98) * mm, "radius": 3 * mm});
            skCircle(sketch, "E2.18.3.0", {"center": v(475, 107.98) * mm, "radius": 3 * mm});
            skCircle(sketch, "E2.18.4.0", {"center": v(475, 132.98) * mm, "radius": 3 * mm});
            skCircle(sketch, "E2.18.5.0", {"center": v(475, 157.98) * mm, "radius": 3 * mm});
            skCircle(sketch, "E2.18.6.0", {"center": v(475, 182.98) * mm, "radius": 3 * mm});
            skCircle(sketch, "E2.18.7.0", {"center": v(475, 207.98) * mm, "radius": 3 * mm});
            skCircle(sketch, "E2.18.8.0", {"center": v(475, 232.98) * mm, "radius": 3 * mm});
            skCircle(sketch, "E2.18.9.0", {"center": v(475, 257.98) * mm, "radius": 3 * mm});
            skCircle(sketch, "E2.18.10.0", {"center": v(475, 282.98) * mm, "radius": 3 * mm});
            skCircle(sketch, "E2.18.11.0", {"center": v(475, 307.98) * mm, "radius": 3 * mm});
            skCircle(sketch, "E2.18.12.0", {"center": v(475, 332.98) * mm, "radius": 3 * mm});
            skCircle(sketch, "E2.18.13.0", {"center": v(475, 357.98) * mm, "radius": 3 * mm});
            skCircle(sketch, "E2.18.14.0", {"center": v(475, 382.98) * mm, "radius": 3 * mm});
            skCircle(sketch, "E2.18.15.0", {"center": v(475, 407.98) * mm, "radius": 3 * mm});
            skCircle(sketch, "E2.18.16.0", {"center": v(475, 432.98) * mm, "radius": 3 * mm});
            skCircle(sketch, "E2.18.17.0", {"center": v(475, 457.98) * mm, "radius": 3 * mm});
            skCircle(sketch, "E2.18.18.0", {"center": v(475, 482.98) * mm, "radius": 3 * mm});
            skCircle(sketch, "E2.18.19.0", {"center": v(475, 507.98) * mm, "radius": 3 * mm});
            skCircle(sketch, "E2.18.20.0", {"center": v(475, 532.98) * mm, "radius": 3 * mm});
            skCircle(sketch, "E2.18.21.0", {"center": v(475, 557.98) * mm, "radius": 3 * mm});
            skCircle(sketch, "E2.18.22.0", {"center": v(475, 582.98) * mm, "radius": 3 * mm});
            skCircle(sketch, "E2.19.0.0", {"center": v(500, 32.98) * mm, "radius": 3 * mm});
            skCircle(sketch, "E2.19.1.0", {"center": v(500, 57.98) * mm, "radius": 3 * mm});
            skCircle(sketch, "E2.19.2.0", {"center": v(500, 82.98) * mm, "radius": 3 * mm});
            skCircle(sketch, "E2.19.3.0", {"center": v(500, 107.98) * mm, "radius": 3 * mm});
            skCircle(sketch, "E2.19.4.0", {"center": v(500, 132.98) * mm, "radius": 3 * mm});
            skCircle(sketch, "E2.19.5.0", {"center": v(500, 157.98) * mm, "radius": 3 * mm});
            skCircle(sketch, "E2.19.6.0", {"center": v(500, 182.98) * mm, "radius": 3 * mm});
            skCircle(sketch, "E2.19.7.0", {"center": v(500, 207.98) * mm, "radius": 3 * mm});
            skCircle(sketch, "E2.19.8.0", {"center": v(500, 232.98) * mm, "radius": 3 * mm});
            skCircle(sketch, "E2.19.9.0", {"center": v(500, 257.98) * mm, "radius": 3 * mm});
            skCircle(sketch, "E2.19.10.0", {"center": v(500, 282.98) * mm, "radius": 3 * mm});
            skCircle(sketch, "E2.19.11.0", {"center": v(500, 307.98) * mm, "radius": 3 * mm});
            skCircle(sketch, "E2.19.12.0", {"center": v(500, 332.98) * mm, "radius": 3 * mm});
            skCircle(sketch, "E2.19.13.0", {"center": v(500, 357.98) * mm, "radius": 3 * mm});
            skCircle(sketch, "E2.19.14.0", {"center": v(500, 382.98) * mm, "radius": 3 * mm});
            skCircle(sketch, "E2.19.15.0", {"center": v(500, 407.98) * mm, "radius": 3 * mm});
            skCircle(sketch, "E2.19.16.0", {"center": v(500, 432.98) * mm, "radius": 3 * mm});
            skCircle(sketch, "E2.19.17.0", {"center": v(500, 457.98) * mm, "radius": 3 * mm});
            skCircle(sketch, "E2.19.18.0", {"center": v(500, 482.98) * mm, "radius": 3 * mm});
            skCircle(sketch, "E2.19.19.0", {"center": v(500, 507.98) * mm, "radius": 3 * mm});
            skCircle(sketch, "E2.19.20.0", {"center": v(500, 532.98) * mm, "radius": 3 * mm});
            skCircle(sketch, "E2.19.21.0", {"center": v(500, 557.98) * mm, "radius": 3 * mm});
            skCircle(sketch, "E2.19.22.0", {"center": v(500, 582.98) * mm, "radius": 3 * mm});
            skCircle(sketch, "E2.20.0.0", {"center": v(525, 32.98) * mm, "radius": 3 * mm});
            skCircle(sketch, "E2.20.1.0", {"center": v(525, 57.98) * mm, "radius": 3 * mm});
            skCircle(sketch, "E2.20.2.0", {"center": v(525, 82.98) * mm, "radius": 3 * mm});
            skCircle(sketch, "E2.20.3.0", {"center": v(525, 107.98) * mm, "radius": 3 * mm});
            skCircle(sketch, "E2.20.4.0", {"center": v(525, 132.98) * mm, "radius": 3 * mm});
            skCircle(sketch, "E2.20.5.0", {"center": v(525, 157.98) * mm, "radius": 3 * mm});
            skCircle(sketch, "E2.20.6.0", {"center": v(525, 182.98) * mm, "radius": 3 * mm});
            skCircle(sketch, "E2.20.7.0", {"center": v(525, 207.98) * mm, "radius": 3 * mm});
            skCircle(sketch, "E2.20.8.0", {"center": v(525, 232.98) * mm, "radius": 3 * mm});
            skCircle(sketch, "E2.20.9.0", {"center": v(525, 257.98) * mm, "radius": 3 * mm});
            skCircle(sketch, "E2.20.10.0", {"center": v(525, 282.98) * mm, "radius": 3 * mm});
            skCircle(sketch, "E2.20.11.0", {"center": v(525, 307.98) * mm, "radius": 3 * mm});
            skCircle(sketch, "E2.20.12.0", {"center": v(525, 332.98) * mm, "radius": 3 * mm});
            skCircle(sketch, "E2.20.13.0", {"center": v(525, 357.98) * mm, "radius": 3 * mm});
            skCircle(sketch, "E2.20.14.0", {"center": v(525, 382.98) * mm, "radius": 3 * mm});
            skCircle(sketch, "E2.20.15.0", {"center": v(525, 407.98) * mm, "radius": 3 * mm});
            skCircle(sketch, "E2.20.16.0", {"center": v(525, 432.98) * mm, "radius": 3 * mm});
            skCircle(sketch, "E2.20.17.0", {"center": v(525, 457.98) * mm, "radius": 3 * mm});
            skCircle(sketch, "E2.20.18.0", {"center": v(525, 482.98) * mm, "radius": 3 * mm});
            skCircle(sketch, "E2.20.19.0", {"center": v(525, 507.98) * mm, "radius": 3 * mm});
            skCircle(sketch, "E2.20.20.0", {"center": v(525, 532.98) * mm, "radius": 3 * mm});
            skCircle(sketch, "E2.20.21.0", {"center": v(525, 557.98) * mm, "radius": 3 * mm});
            skCircle(sketch, "E2.20.22.0", {"center": v(525, 582.98) * mm, "radius": 3 * mm});
            skCircle(sketch, "E2.21.0.0", {"center": v(550, 32.98) * mm, "radius": 3 * mm});
            skCircle(sketch, "E2.21.1.0", {"center": v(550, 57.98) * mm, "radius": 3 * mm});
            skCircle(sketch, "E2.21.2.0", {"center": v(550, 82.98) * mm, "radius": 3 * mm});
            skCircle(sketch, "E2.21.3.0", {"center": v(550, 107.98) * mm, "radius": 3 * mm});
            skCircle(sketch, "E2.21.4.0", {"center": v(550, 132.98) * mm, "radius": 3 * mm});
            skCircle(sketch, "E2.21.5.0", {"center": v(550, 157.98) * mm, "radius": 3 * mm});
            skCircle(sketch, "E2.21.6.0", {"center": v(550, 182.98) * mm, "radius": 3 * mm});
            skCircle(sketch, "E2.21.7.0", {"center": v(550, 207.98) * mm, "radius": 3 * mm});
            skCircle(sketch, "E2.21.8.0", {"center": v(550, 232.98) * mm, "radius": 3 * mm});
            skCircle(sketch, "E2.21.9.0", {"center": v(550, 257.98) * mm, "radius": 3 * mm});
            skCircle(sketch, "E2.21.10.0", {"center": v(550, 282.98) * mm, "radius": 3 * mm});
            skCircle(sketch, "E2.21.11.0", {"center": v(550, 307.98) * mm, "radius": 3 * mm});
            skCircle(sketch, "E2.21.12.0", {"center": v(550, 332.98) * mm, "radius": 3 * mm});
            skCircle(sketch, "E2.21.13.0", {"center": v(550, 357.98) * mm, "radius": 3 * mm});
            skCircle(sketch, "E2.21.14.0", {"center": v(550, 382.98) * mm, "radius": 3 * mm});
            skCircle(sketch, "E2.21.15.0", {"center": v(550, 407.98) * mm, "radius": 3 * mm});
            skCircle(sketch, "E2.21.16.0", {"center": v(550, 432.98) * mm, "radius": 3 * mm});
            skCircle(sketch, "E2.21.17.0", {"center": v(550, 457.98) * mm, "radius": 3 * mm});
            skCircle(sketch, "E2.21.18.0", {"center": v(550, 482.98) * mm, "radius": 3 * mm});
            skCircle(sketch, "E2.21.19.0", {"center": v(550, 507.98) * mm, "radius": 3 * mm});
            skCircle(sketch, "E2.21.20.0", {"center": v(550, 532.98) * mm, "radius": 3 * mm});
            skCircle(sketch, "E2.21.21.0", {"center": v(550, 557.98) * mm, "radius": 3 * mm});
            skCircle(sketch, "E2.21.22.0", {"center": v(550, 582.98) * mm, "radius": 3 * mm});
            skCircle(sketch, "E2.22.0.0", {"center": v(575, 32.98) * mm, "radius": 3 * mm});
            skCircle(sketch, "E2.22.1.0", {"center": v(575, 57.98) * mm, "radius": 3 * mm});
            skCircle(sketch, "E2.22.2.0", {"center": v(575, 82.98) * mm, "radius": 3 * mm});
            skCircle(sketch, "E2.22.3.0", {"center": v(575, 107.98) * mm, "radius": 3 * mm});
            skCircle(sketch, "E2.22.4.0", {"center": v(575, 132.98) * mm, "radius": 3 * mm});
            skCircle(sketch, "E2.22.5.0", {"center": v(575, 157.98) * mm, "radius": 3 * mm});
            skCircle(sketch, "E2.22.6.0", {"center": v(575, 182.98) * mm, "radius": 3 * mm});
            skCircle(sketch, "E2.22.7.0", {"center": v(575, 207.98) * mm, "radius": 3 * mm});
            skCircle(sketch, "E2.22.8.0", {"center": v(575, 232.98) * mm, "radius": 3 * mm});
            skCircle(sketch, "E2.22.9.0", {"center": v(575, 257.98) * mm, "radius": 3 * mm});
            skCircle(sketch, "E2.22.10.0", {"center": v(575, 282.98) * mm, "radius": 3 * mm});
            skCircle(sketch, "E2.22.11.0", {"center": v(575, 307.98) * mm, "radius": 3 * mm});
            skCircle(sketch, "E2.22.12.0", {"center": v(575, 332.98) * mm, "radius": 3 * mm});
            skCircle(sketch, "E2.22.13.0", {"center": v(575, 357.98) * mm, "radius": 3 * mm});
            skCircle(sketch, "E2.22.14.0", {"center": v(575, 382.98) * mm, "radius": 3 * mm});
            skCircle(sketch, "E2.22.15.0", {"center": v(575, 407.98) * mm, "radius": 3 * mm});
            skCircle(sketch, "E2.22.16.0", {"center": v(575, 432.98) * mm, "radius": 3 * mm});
            skCircle(sketch, "E2.22.17.0", {"center": v(575, 457.98) * mm, "radius": 3 * mm});
            skCircle(sketch, "E2.22.18.0", {"center": v(575, 482.98) * mm, "radius": 3 * mm});
            skCircle(sketch, "E2.22.19.0", {"center": v(575, 507.98) * mm, "radius": 3 * mm});
            skCircle(sketch, "E2.22.20.0", {"center": v(575, 532.98) * mm, "radius": 3 * mm});
            skCircle(sketch, "E2.22.21.0", {"center": v(575, 557.98) * mm, "radius": 3 * mm});
            skCircle(sketch, "E2.22.22.0", {"center": v(575, 582.98) * mm, "radius": 3 * mm});
            skCircle(sketch, "E2.23.0.0", {"center": v(600, 32.98) * mm, "radius": 3 * mm});
            skCircle(sketch, "E2.23.1.0", {"center": v(600, 57.98) * mm, "radius": 3 * mm});
            skCircle(sketch, "E2.23.2.0", {"center": v(600, 82.98) * mm, "radius": 3 * mm});
            skCircle(sketch, "E2.23.3.0", {"center": v(600, 107.98) * mm, "radius": 3 * mm});
            skCircle(sketch, "E2.23.4.0", {"center": v(600, 132.98) * mm, "radius": 3 * mm});
            skCircle(sketch, "E2.23.5.0", {"center": v(600, 157.98) * mm, "radius": 3 * mm});
            skCircle(sketch, "E2.23.6.0", {"center": v(600, 182.98) * mm, "radius": 3 * mm});
            skCircle(sketch, "E2.23.7.0", {"center": v(600, 207.98) * mm, "radius": 3 * mm});
            skCircle(sketch, "E2.23.8.0", {"center": v(600, 232.98) * mm, "radius": 3 * mm});
            skCircle(sketch, "E2.23.9.0", {"center": v(600, 257.98) * mm, "radius": 3 * mm});
            skCircle(sketch, "E2.23.10.0", {"center": v(600, 282.98) * mm, "radius": 3 * mm});
            skCircle(sketch, "E2.23.11.0", {"center": v(600, 307.98) * mm, "radius": 3 * mm});
            skCircle(sketch, "E2.23.12.0", {"center": v(600, 332.98) * mm, "radius": 3 * mm});
            skCircle(sketch, "E2.23.13.0", {"center": v(600, 357.98) * mm, "radius": 3 * mm});
            skCircle(sketch, "E2.23.14.0", {"center": v(600, 382.98) * mm, "radius": 3 * mm});
            skCircle(sketch, "E2.23.15.0", {"center": v(600, 407.98) * mm, "radius": 3 * mm});
            skCircle(sketch, "E2.23.16.0", {"center": v(600, 432.98) * mm, "radius": 3 * mm});
            skCircle(sketch, "E2.23.17.0", {"center": v(600, 457.98) * mm, "radius": 3 * mm});
            skCircle(sketch, "E2.23.18.0", {"center": v(600, 482.98) * mm, "radius": 3 * mm});
            skCircle(sketch, "E2.23.19.0", {"center": v(600, 507.98) * mm, "radius": 3 * mm});
            skCircle(sketch, "E2.23.20.0", {"center": v(600, 532.98) * mm, "radius": 3 * mm});
            skCircle(sketch, "E2.23.21.0", {"center": v(600, 557.98) * mm, "radius": 3 * mm});
            skCircle(sketch, "E2.23.22.0", {"center": v(600, 582.98) * mm, "radius": 3 * mm});
            skCircle(sketch, "E2.24.0.0", {"center": v(625, 32.98) * mm, "radius": 3 * mm});
            skCircle(sketch, "E2.24.1.0", {"center": v(625, 57.98) * mm, "radius": 3 * mm});
            skCircle(sketch, "E2.24.2.0", {"center": v(625, 82.98) * mm, "radius": 3 * mm});
            skCircle(sketch, "E2.24.3.0", {"center": v(625, 107.98) * mm, "radius": 3 * mm});
            skCircle(sketch, "E2.24.4.0", {"center": v(625, 132.98) * mm, "radius": 3 * mm});
            skCircle(sketch, "E2.24.5.0", {"center": v(625, 157.98) * mm, "radius": 3 * mm});
            skCircle(sketch, "E2.24.6.0", {"center": v(625, 182.98) * mm, "radius": 3 * mm});
            skCircle(sketch, "E2.24.7.0", {"center": v(625, 207.98) * mm, "radius": 3 * mm});
            skCircle(sketch, "E2.24.8.0", {"center": v(625, 232.98) * mm, "radius": 3 * mm});
            skCircle(sketch, "E2.24.9.0", {"center": v(625, 257.98) * mm, "radius": 3 * mm});
            skCircle(sketch, "E2.24.10.0", {"center": v(625, 282.98) * mm, "radius": 3 * mm});
            skCircle(sketch, "E2.24.11.0", {"center": v(625, 307.98) * mm, "radius": 3 * mm});
            skCircle(sketch, "E2.24.12.0", {"center": v(625, 332.98) * mm, "radius": 3 * mm});
            skCircle(sketch, "E2.24.13.0", {"center": v(625, 357.98) * mm, "radius": 3 * mm});
            skCircle(sketch, "E2.24.14.0", {"center": v(625, 382.98) * mm, "radius": 3 * mm});
            skCircle(sketch, "E2.24.15.0", {"center": v(625, 407.98) * mm, "radius": 3 * mm});
            skCircle(sketch, "E2.24.16.0", {"center": v(625, 432.98) * mm, "radius": 3 * mm});
            skCircle(sketch, "E2.24.17.0", {"center": v(625, 457.98) * mm, "radius": 3 * mm});
            skCircle(sketch, "E2.24.18.0", {"center": v(625, 482.98) * mm, "radius": 3 * mm});
            skCircle(sketch, "E2.24.19.0", {"center": v(625, 507.98) * mm, "radius": 3 * mm});
            skCircle(sketch, "E2.24.20.0", {"center": v(625, 532.98) * mm, "radius": 3 * mm});
            skCircle(sketch, "E2.24.21.0", {"center": v(625, 557.98) * mm, "radius": 3 * mm});
            skCircle(sketch, "E2.24.22.0", {"center": v(625, 582.98) * mm, "radius": 3 * mm});
            skCircle(sketch, "E2.25.0.0", {"center": v(650, 32.98) * mm, "radius": 3 * mm});
            skCircle(sketch, "E2.25.1.0", {"center": v(650, 57.98) * mm, "radius": 3 * mm});
            skCircle(sketch, "E2.25.2.0", {"center": v(650, 82.98) * mm, "radius": 3 * mm});
            skCircle(sketch, "E2.25.3.0", {"center": v(650, 107.98) * mm, "radius": 3 * mm});
            skCircle(sketch, "E2.25.4.0", {"center": v(650, 132.98) * mm, "radius": 3 * mm});
            skCircle(sketch, "E2.25.5.0", {"center": v(650, 157.98) * mm, "radius": 3 * mm});
            skCircle(sketch, "E2.25.6.0", {"center": v(650, 182.98) * mm, "radius": 3 * mm});
            skCircle(sketch, "E2.25.7.0", {"center": v(650, 207.98) * mm, "radius": 3 * mm});
            skCircle(sketch, "E2.25.8.0", {"center": v(650, 232.98) * mm, "radius": 3 * mm});
            skCircle(sketch, "E2.25.9.0", {"center": v(650, 257.98) * mm, "radius": 3 * mm});
            skCircle(sketch, "E2.25.10.0", {"center": v(650, 282.98) * mm, "radius": 3 * mm});
            skCircle(sketch, "E2.25.11.0", {"center": v(650, 307.98) * mm, "radius": 3 * mm});
            skCircle(sketch, "E2.25.12.0", {"center": v(650, 332.98) * mm, "radius": 3 * mm});
            skCircle(sketch, "E2.25.13.0", {"center": v(650, 357.98) * mm, "radius": 3 * mm});
            skCircle(sketch, "E2.25.14.0", {"center": v(650, 382.98) * mm, "radius": 3 * mm});
            skCircle(sketch, "E2.25.15.0", {"center": v(650, 407.98) * mm, "radius": 3 * mm});
            skCircle(sketch, "E2.25.16.0", {"center": v(650, 432.98) * mm, "radius": 3 * mm});
            skCircle(sketch, "E2.25.17.0", {"center": v(650, 457.98) * mm, "radius": 3 * mm});
            skCircle(sketch, "E2.25.18.0", {"center": v(650, 482.98) * mm, "radius": 3 * mm});
            skCircle(sketch, "E2.25.19.0", {"center": v(650, 507.98) * mm, "radius": 3 * mm});
            skCircle(sketch, "E2.25.20.0", {"center": v(650, 532.98) * mm, "radius": 3 * mm});
            skCircle(sketch, "E2.25.21.0", {"center": v(650, 557.98) * mm, "radius": 3 * mm});
            skCircle(sketch, "E2.25.22.0", {"center": v(650, 582.98) * mm, "radius": 3 * mm});
            skCircle(sketch, "E2.26.0.0", {"center": v(675, 32.98) * mm, "radius": 3 * mm});
            skCircle(sketch, "E2.26.1.0", {"center": v(675, 57.98) * mm, "radius": 3 * mm});
            skCircle(sketch, "E2.26.2.0", {"center": v(675, 82.98) * mm, "radius": 3 * mm});
            skCircle(sketch, "E2.26.3.0", {"center": v(675, 107.98) * mm, "radius": 3 * mm});
            skCircle(sketch, "E2.26.4.0", {"center": v(675, 132.98) * mm, "radius": 3 * mm});
            skCircle(sketch, "E2.26.5.0", {"center": v(675, 157.98) * mm, "radius": 3 * mm});
            skCircle(sketch, "E2.26.6.0", {"center": v(675, 182.98) * mm, "radius": 3 * mm});
            skCircle(sketch, "E2.26.7.0", {"center": v(675, 207.98) * mm, "radius": 3 * mm});
            skCircle(sketch, "E2.26.8.0", {"center": v(675, 232.98) * mm, "radius": 3 * mm});
            skCircle(sketch, "E2.26.9.0", {"center": v(675, 257.98) * mm, "radius": 3 * mm});
            skCircle(sketch, "E2.26.10.0", {"center": v(675, 282.98) * mm, "radius": 3 * mm});
            skCircle(sketch, "E2.26.11.0", {"center": v(675, 307.98) * mm, "radius": 3 * mm});
            skCircle(sketch, "E2.26.12.0", {"center": v(675, 332.98) * mm, "radius": 3 * mm});
            skCircle(sketch, "E2.26.13.0", {"center": v(675, 357.98) * mm, "radius": 3 * mm});
            skCircle(sketch, "E2.26.14.0", {"center": v(675, 382.98) * mm, "radius": 3 * mm});
            skCircle(sketch, "E2.26.15.0", {"center": v(675, 407.98) * mm, "radius": 3 * mm});
            skCircle(sketch, "E2.26.16.0", {"center": v(675, 432.98) * mm, "radius": 3 * mm});
            skCircle(sketch, "E2.26.17.0", {"center": v(675, 457.98) * mm, "radius": 3 * mm});
            skCircle(sketch, "E2.26.18.0", {"center": v(675, 482.98) * mm, "radius": 3 * mm});
            skCircle(sketch, "E2.26.19.0", {"center": v(675, 507.98) * mm, "radius": 3 * mm});
            skCircle(sketch, "E2.26.20.0", {"center": v(675, 532.98) * mm, "radius": 3 * mm});
            skCircle(sketch, "E2.26.21.0", {"center": v(675, 557.98) * mm, "radius": 3 * mm});
            skCircle(sketch, "E2.26.22.0", {"center": v(675, 582.98) * mm, "radius": 3 * mm});
            skCircle(sketch, "E2.27.0.0", {"center": v(700, 32.98) * mm, "radius": 3 * mm});
            skCircle(sketch, "E2.27.1.0", {"center": v(700, 57.98) * mm, "radius": 3 * mm});
            skCircle(sketch, "E2.27.2.0", {"center": v(700, 82.98) * mm, "radius": 3 * mm});
            skCircle(sketch, "E2.27.3.0", {"center": v(700, 107.98) * mm, "radius": 3 * mm});
            skCircle(sketch, "E2.27.4.0", {"center": v(700, 132.98) * mm, "radius": 3 * mm});
            skCircle(sketch, "E2.27.5.0", {"center": v(700, 157.98) * mm, "radius": 3 * mm});
            skCircle(sketch, "E2.27.6.0", {"center": v(700, 182.98) * mm, "radius": 3 * mm});
            skCircle(sketch, "E2.27.7.0", {"center": v(700, 207.98) * mm, "radius": 3 * mm});
            skCircle(sketch, "E2.27.8.0", {"center": v(700, 232.98) * mm, "radius": 3 * mm});
            skCircle(sketch, "E2.27.9.0", {"center": v(700, 257.98) * mm, "radius": 3 * mm});
            skCircle(sketch, "E2.27.10.0", {"center": v(700, 282.98) * mm, "radius": 3 * mm});
            skCircle(sketch, "E2.27.11.0", {"center": v(700, 307.98) * mm, "radius": 3 * mm});
            skCircle(sketch, "E2.27.12.0", {"center": v(700, 332.98) * mm, "radius": 3 * mm});
            skCircle(sketch, "E2.27.13.0", {"center": v(700, 357.98) * mm, "radius": 3 * mm});
            skCircle(sketch, "E2.27.14.0", {"center": v(700, 382.98) * mm, "radius": 3 * mm});
            skCircle(sketch, "E2.27.15.0", {"center": v(700, 407.98) * mm, "radius": 3 * mm});
            skCircle(sketch, "E2.27.16.0", {"center": v(700, 432.98) * mm, "radius": 3 * mm});
            skCircle(sketch, "E2.27.17.0", {"center": v(700, 457.98) * mm, "radius": 3 * mm});
            skCircle(sketch, "E2.27.18.0", {"center": v(700, 482.98) * mm, "radius": 3 * mm});
            skCircle(sketch, "E2.27.19.0", {"center": v(700, 507.98) * mm, "radius": 3 * mm});
            skCircle(sketch, "E2.27.20.0", {"center": v(700, 532.98) * mm, "radius": 3 * mm});
            skCircle(sketch, "E2.27.21.0", {"center": v(700, 557.98) * mm, "radius": 3 * mm});
            skCircle(sketch, "E2.27.22.0", {"center": v(700, 582.98) * mm, "radius": 3 * mm});
            skCircle(sketch, "E2.28.0.0", {"center": v(725, 32.98) * mm, "radius": 3 * mm});
            skCircle(sketch, "E2.28.1.0", {"center": v(725, 57.98) * mm, "radius": 3 * mm});
            skCircle(sketch, "E2.28.2.0", {"center": v(725, 82.98) * mm, "radius": 3 * mm});
            skCircle(sketch, "E2.28.3.0", {"center": v(725, 107.98) * mm, "radius": 3 * mm});
            skCircle(sketch, "E2.28.4.0", {"center": v(725, 132.98) * mm, "radius": 3 * mm});
            skCircle(sketch, "E2.28.5.0", {"center": v(725, 157.98) * mm, "radius": 3 * mm});
            skCircle(sketch, "E2.28.6.0", {"center": v(725, 182.98) * mm, "radius": 3 * mm});
            skCircle(sketch, "E2.28.7.0", {"center": v(725, 207.98) * mm, "radius": 3 * mm});
            skCircle(sketch, "E2.28.8.0", {"center": v(725, 232.98) * mm, "radius": 3 * mm});
            skCircle(sketch, "E2.28.9.0", {"center": v(725, 257.98) * mm, "radius": 3 * mm});
            skCircle(sketch, "E2.28.10.0", {"center": v(725, 282.98) * mm, "radius": 3 * mm});
            skCircle(sketch, "E2.28.11.0", {"center": v(725, 307.98) * mm, "radius": 3 * mm});
            skCircle(sketch, "E2.28.12.0", {"center": v(725, 332.98) * mm, "radius": 3 * mm});
            skCircle(sketch, "E2.28.13.0", {"center": v(725, 357.98) * mm, "radius": 3 * mm});
            skCircle(sketch, "E2.28.14.0", {"center": v(725, 382.98) * mm, "radius": 3 * mm});
            skCircle(sketch, "E2.28.15.0", {"center": v(725, 407.98) * mm, "radius": 3 * mm});
            skCircle(sketch, "E2.28.16.0", {"center": v(725, 432.98) * mm, "radius": 3 * mm});
            skCircle(sketch, "E2.28.17.0", {"center": v(725, 457.98) * mm, "radius": 3 * mm});
            skCircle(sketch, "E2.28.18.0", {"center": v(725, 482.98) * mm, "radius": 3 * mm});
            skCircle(sketch, "E2.28.19.0", {"center": v(725, 507.98) * mm, "radius": 3 * mm});
            skCircle(sketch, "E2.28.20.0", {"center": v(725, 532.98) * mm, "radius": 3 * mm});
            skCircle(sketch, "E2.28.21.0", {"center": v(725, 557.98) * mm, "radius": 3 * mm});
            skCircle(sketch, "E2.28.22.0", {"center": v(725, 582.98) * mm, "radius": 3 * mm});
            skCircle(sketch, "E2.29.0.0", {"center": v(750, 32.98) * mm, "radius": 3 * mm});
            skCircle(sketch, "E2.29.1.0", {"center": v(750, 57.98) * mm, "radius": 3 * mm});
            skCircle(sketch, "E2.29.2.0", {"center": v(750, 82.98) * mm, "radius": 3 * mm});
            skCircle(sketch, "E2.29.3.0", {"center": v(750, 107.98) * mm, "radius": 3 * mm});
            skCircle(sketch, "E2.29.4.0", {"center": v(750, 132.98) * mm, "radius": 3 * mm});
            skCircle(sketch, "E2.29.5.0", {"center": v(750, 157.98) * mm, "radius": 3 * mm});
            skCircle(sketch, "E2.29.6.0", {"center": v(750, 182.98) * mm, "radius": 3 * mm});
            skCircle(sketch, "E2.29.7.0", {"center": v(750, 207.98) * mm, "radius": 3 * mm});
            skCircle(sketch, "E2.29.8.0", {"center": v(750, 232.98) * mm, "radius": 3 * mm});
            skCircle(sketch, "E2.29.9.0", {"center": v(750, 257.98) * mm, "radius": 3 * mm});
            skCircle(sketch, "E2.29.10.0", {"center": v(750, 282.98) * mm, "radius": 3 * mm});
            skCircle(sketch, "E2.29.11.0", {"center": v(750, 307.98) * mm, "radius": 3 * mm});
            skCircle(sketch, "E2.29.12.0", {"center": v(750, 332.98) * mm, "radius": 3 * mm});
            skCircle(sketch, "E2.29.13.0", {"center": v(750, 357.98) * mm, "radius": 3 * mm});
            skCircle(sketch, "E2.29.14.0", {"center": v(750, 382.98) * mm, "radius": 3 * mm});
            skCircle(sketch, "E2.29.15.0", {"center": v(750, 407.98) * mm, "radius": 3 * mm});
            skCircle(sketch, "E2.29.16.0", {"center": v(750, 432.98) * mm, "radius": 3 * mm});
            skCircle(sketch, "E2.29.17.0", {"center": v(750, 457.98) * mm, "radius": 3 * mm});
            skCircle(sketch, "E2.29.18.0", {"center": v(750, 482.98) * mm, "radius": 3 * mm});
            skCircle(sketch, "E2.29.19.0", {"center": v(750, 507.98) * mm, "radius": 3 * mm});
            skCircle(sketch, "E2.29.20.0", {"center": v(750, 532.98) * mm, "radius": 3 * mm});
            skCircle(sketch, "E2.29.21.0", {"center": v(750, 557.98) * mm, "radius": 3 * mm});
            skCircle(sketch, "E2.29.22.0", {"center": v(750, 582.98) * mm, "radius": 3 * mm});
            skCircle(sketch, "E2.30.0.0", {"center": v(775, 32.98) * mm, "radius": 3 * mm});
            skCircle(sketch, "E2.30.1.0", {"center": v(775, 57.98) * mm, "radius": 3 * mm});
            skCircle(sketch, "E2.30.2.0", {"center": v(775, 82.98) * mm, "radius": 3 * mm});
            skCircle(sketch, "E2.30.3.0", {"center": v(775, 107.98) * mm, "radius": 3 * mm});
            skCircle(sketch, "E2.30.4.0", {"center": v(775, 132.98) * mm, "radius": 3 * mm});
            skCircle(sketch, "E2.30.5.0", {"center": v(775, 157.98) * mm, "radius": 3 * mm});
            skCircle(sketch, "E2.30.6.0", {"center": v(775, 182.98) * mm, "radius": 3 * mm});
            skCircle(sketch, "E2.30.7.0", {"center": v(775, 207.98) * mm, "radius": 3 * mm});
            skCircle(sketch, "E2.30.8.0", {"center": v(775, 232.98) * mm, "radius": 3 * mm});
            skCircle(sketch, "E2.30.9.0", {"center": v(775, 257.98) * mm, "radius": 3 * mm});
            skCircle(sketch, "E2.30.10.0", {"center": v(775, 282.98) * mm, "radius": 3 * mm});
            skCircle(sketch, "E2.30.11.0", {"center": v(775, 307.98) * mm, "radius": 3 * mm});
            skCircle(sketch, "E2.30.12.0", {"center": v(775, 332.98) * mm, "radius": 3 * mm});
            skCircle(sketch, "E2.30.13.0", {"center": v(775, 357.98) * mm, "radius": 3 * mm});
            skCircle(sketch, "E2.30.14.0", {"center": v(775, 382.98) * mm, "radius": 3 * mm});
            skCircle(sketch, "E2.30.15.0", {"center": v(775, 407.98) * mm, "radius": 3 * mm});
            skCircle(sketch, "E2.30.16.0", {"center": v(775, 432.98) * mm, "radius": 3 * mm});
            skCircle(sketch, "E2.30.17.0", {"center": v(775, 457.98) * mm, "radius": 3 * mm});
            skCircle(sketch, "E2.30.18.0", {"center": v(775, 482.98) * mm, "radius": 3 * mm});
            skCircle(sketch, "E2.30.19.0", {"center": v(775, 507.98) * mm, "radius": 3 * mm});
            skCircle(sketch, "E2.30.20.0", {"center": v(775, 532.98) * mm, "radius": 3 * mm});
            skCircle(sketch, "E2.30.21.0", {"center": v(775, 557.98) * mm, "radius": 3 * mm});
            skCircle(sketch, "E2.30.22.0", {"center": v(775, 582.98) * mm, "radius": 3 * mm});
            skCircle(sketch, "E2.31.0.0", {"center": v(800, 32.98) * mm, "radius": 3 * mm});
            skCircle(sketch, "E2.31.1.0", {"center": v(800, 57.98) * mm, "radius": 3 * mm});
            skCircle(sketch, "E2.31.2.0", {"center": v(800, 82.98) * mm, "radius": 3 * mm});
            skCircle(sketch, "E2.31.3.0", {"center": v(800, 107.98) * mm, "radius": 3 * mm});
            skCircle(sketch, "E2.31.4.0", {"center": v(800, 132.98) * mm, "radius": 3 * mm});
            skCircle(sketch, "E2.31.5.0", {"center": v(800, 157.98) * mm, "radius": 3 * mm});
            skCircle(sketch, "E2.31.6.0", {"center": v(800, 182.98) * mm, "radius": 3 * mm});
            skCircle(sketch, "E2.31.7.0", {"center": v(800, 207.98) * mm, "radius": 3 * mm});
            skCircle(sketch, "E2.31.8.0", {"center": v(800, 232.98) * mm, "radius": 3 * mm});
            skCircle(sketch, "E2.31.9.0", {"center": v(800, 257.98) * mm, "radius": 3 * mm});
            skCircle(sketch, "E2.31.10.0", {"center": v(800, 282.98) * mm, "radius": 3 * mm});
            skCircle(sketch, "E2.31.11.0", {"center": v(800, 307.98) * mm, "radius": 3 * mm});
            skCircle(sketch, "E2.31.12.0", {"center": v(800, 332.98) * mm, "radius": 3 * mm});
            skCircle(sketch, "E2.31.13.0", {"center": v(800, 357.98) * mm, "radius": 3 * mm});
            skCircle(sketch, "E2.31.14.0", {"center": v(800, 382.98) * mm, "radius": 3 * mm});
            skCircle(sketch, "E2.31.15.0", {"center": v(800, 407.98) * mm, "radius": 3 * mm});
            skCircle(sketch, "E2.31.16.0", {"center": v(800, 432.98) * mm, "radius": 3 * mm});
            skCircle(sketch, "E2.31.17.0", {"center": v(800, 457.98) * mm, "radius": 3 * mm});
            skCircle(sketch, "E2.31.18.0", {"center": v(800, 482.98) * mm, "radius": 3 * mm});
            skCircle(sketch, "E2.31.19.0", {"center": v(800, 507.98) * mm, "radius": 3 * mm});
            skCircle(sketch, "E2.31.20.0", {"center": v(800, 532.98) * mm, "radius": 3 * mm});
            skCircle(sketch, "E2.31.21.0", {"center": v(800, 557.98) * mm, "radius": 3 * mm});
            skCircle(sketch, "E2.31.22.0", {"center": v(800, 582.98) * mm, "radius": 3 * mm});
            skCircle(sketch, "E2.32.0.0", {"center": v(825, 32.98) * mm, "radius": 3 * mm});
            skCircle(sketch, "E2.32.1.0", {"center": v(825, 57.98) * mm, "radius": 3 * mm});
            skCircle(sketch, "E2.32.2.0", {"center": v(825, 82.98) * mm, "radius": 3 * mm});
            skCircle(sketch, "E2.32.3.0", {"center": v(825, 107.98) * mm, "radius": 3 * mm});
            skCircle(sketch, "E2.32.4.0", {"center": v(825, 132.98) * mm, "radius": 3 * mm});
            skCircle(sketch, "E2.32.5.0", {"center": v(825, 157.98) * mm, "radius": 3 * mm});
            skCircle(sketch, "E2.32.6.0", {"center": v(825, 182.98) * mm, "radius": 3 * mm});
            skCircle(sketch, "E2.32.7.0", {"center": v(825, 207.98) * mm, "radius": 3 * mm});
            skCircle(sketch, "E2.32.8.0", {"center": v(825, 232.98) * mm, "radius": 3 * mm});
            skCircle(sketch, "E2.32.9.0", {"center": v(825, 257.98) * mm, "radius": 3 * mm});
            skCircle(sketch, "E2.32.10.0", {"center": v(825, 282.98) * mm, "radius": 3 * mm});
            skCircle(sketch, "E2.32.11.0", {"center": v(825, 307.98) * mm, "radius": 3 * mm});
            skCircle(sketch, "E2.32.12.0", {"center": v(825, 332.98) * mm, "radius": 3 * mm});
            skCircle(sketch, "E2.32.13.0", {"center": v(825, 357.98) * mm, "radius": 3 * mm});
            skCircle(sketch, "E2.32.14.0", {"center": v(825, 382.98) * mm, "radius": 3 * mm});
            skCircle(sketch, "E2.32.15.0", {"center": v(825, 407.98) * mm, "radius": 3 * mm});
            skCircle(sketch, "E2.32.16.0", {"center": v(825, 432.98) * mm, "radius": 3 * mm});
            skCircle(sketch, "E2.32.17.0", {"center": v(825, 457.98) * mm, "radius": 3 * mm});
            skCircle(sketch, "E2.32.18.0", {"center": v(825, 482.98) * mm, "radius": 3 * mm});
            skCircle(sketch, "E2.32.19.0", {"center": v(825, 507.98) * mm, "radius": 3 * mm});
            skCircle(sketch, "E2.32.20.0", {"center": v(825, 532.98) * mm, "radius": 3 * mm});
            skCircle(sketch, "E2.32.21.0", {"center": v(825, 557.98) * mm, "radius": 3 * mm});
            skCircle(sketch, "E2.32.22.0", {"center": v(825, 582.98) * mm, "radius": 3 * mm});
            skCircle(sketch, "E2.33.0.0", {"center": v(850, 32.98) * mm, "radius": 3 * mm});
            skCircle(sketch, "E2.33.1.0", {"center": v(850, 57.98) * mm, "radius": 3 * mm});
            skCircle(sketch, "E2.33.2.0", {"center": v(850, 82.98) * mm, "radius": 3 * mm});
            skCircle(sketch, "E2.33.3.0", {"center": v(850, 107.98) * mm, "radius": 3 * mm});
            skCircle(sketch, "E2.33.4.0", {"center": v(850, 132.98) * mm, "radius": 3 * mm});
            skCircle(sketch, "E2.33.5.0", {"center": v(850, 157.98) * mm, "radius": 3 * mm});
            skCircle(sketch, "E2.33.6.0", {"center": v(850, 182.98) * mm, "radius": 3 * mm});
            skCircle(sketch, "E2.33.7.0", {"center": v(850, 207.98) * mm, "radius": 3 * mm});
            skCircle(sketch, "E2.33.8.0", {"center": v(850, 232.98) * mm, "radius": 3 * mm});
            skCircle(sketch, "E2.33.9.0", {"center": v(850, 257.98) * mm, "radius": 3 * mm});
            skCircle(sketch, "E2.33.10.0", {"center": v(850, 282.98) * mm, "radius": 3 * mm});
            skCircle(sketch, "E2.33.11.0", {"center": v(850, 307.98) * mm, "radius": 3 * mm});
            skCircle(sketch, "E2.33.12.0", {"center": v(850, 332.98) * mm, "radius": 3 * mm});
            skCircle(sketch, "E2.33.13.0", {"center": v(850, 357.98) * mm, "radius": 3 * mm});
            skCircle(sketch, "E2.33.14.0", {"center": v(850, 382.98) * mm, "radius": 3 * mm});
            skCircle(sketch, "E2.33.15.0", {"center": v(850, 407.98) * mm, "radius": 3 * mm});
            skCircle(sketch, "E2.33.16.0", {"center": v(850, 432.98) * mm, "radius": 3 * mm});
            skCircle(sketch, "E2.33.17.0", {"center": v(850, 457.98) * mm, "radius": 3 * mm});
            skCircle(sketch, "E2.33.18.0", {"center": v(850, 482.98) * mm, "radius": 3 * mm});
            skCircle(sketch, "E2.33.19.0", {"center": v(850, 507.98) * mm, "radius": 3 * mm});
            skCircle(sketch, "E2.33.20.0", {"center": v(850, 532.98) * mm, "radius": 3 * mm});
            skCircle(sketch, "E2.33.21.0", {"center": v(850, 557.98) * mm, "radius": 3 * mm});
            skCircle(sketch, "E2.33.22.0", {"center": v(850, 582.98) * mm, "radius": 3 * mm});
            skCircle(sketch, "E2.34.0.0", {"center": v(875, 32.98) * mm, "radius": 3 * mm});
            skCircle(sketch, "E2.34.1.0", {"center": v(875, 57.98) * mm, "radius": 3 * mm});
            skCircle(sketch, "E2.34.2.0", {"center": v(875, 82.98) * mm, "radius": 3 * mm});
            skCircle(sketch, "E2.34.3.0", {"center": v(875, 107.98) * mm, "radius": 3 * mm});
            skCircle(sketch, "E2.34.4.0", {"center": v(875, 132.98) * mm, "radius": 3 * mm});
            skCircle(sketch, "E2.34.5.0", {"center": v(875, 157.98) * mm, "radius": 3 * mm});
            skCircle(sketch, "E2.34.6.0", {"center": v(875, 182.98) * mm, "radius": 3 * mm});
            skCircle(sketch, "E2.34.7.0", {"center": v(875, 207.98) * mm, "radius": 3 * mm});
            skCircle(sketch, "E2.34.8.0", {"center": v(875, 232.98) * mm, "radius": 3 * mm});
            skCircle(sketch, "E2.34.9.0", {"center": v(875, 257.98) * mm, "radius": 3 * mm});
            skCircle(sketch, "E2.34.10.0", {"center": v(875, 282.98) * mm, "radius": 3 * mm});
            skCircle(sketch, "E2.34.11.0", {"center": v(875, 307.98) * mm, "radius": 3 * mm});
            skCircle(sketch, "E2.34.12.0", {"center": v(875, 332.98) * mm, "radius": 3 * mm});
            skCircle(sketch, "E2.34.13.0", {"center": v(875, 357.98) * mm, "radius": 3 * mm});
            skCircle(sketch, "E2.34.14.0", {"center": v(875, 382.98) * mm, "radius": 3 * mm});
            skCircle(sketch, "E2.34.15.0", {"center": v(875, 407.98) * mm, "radius": 3 * mm});
            skCircle(sketch, "E2.34.16.0", {"center": v(875, 432.98) * mm, "radius": 3 * mm});
            skCircle(sketch, "E2.34.17.0", {"center": v(875, 457.98) * mm, "radius": 3 * mm});
            skCircle(sketch, "E2.34.18.0", {"center": v(875, 482.98) * mm, "radius": 3 * mm});
            skCircle(sketch, "E2.34.19.0", {"center": v(875, 507.98) * mm, "radius": 3 * mm});
            skCircle(sketch, "E2.34.20.0", {"center": v(875, 532.98) * mm, "radius": 3 * mm});
            skCircle(sketch, "E2.34.21.0", {"center": v(875, 557.98) * mm, "radius": 3 * mm});
            skCircle(sketch, "E2.34.22.0", {"center": v(875, 582.98) * mm, "radius": 3 * mm});
            skLineSegment(sketch, "E2.direction1", {"start": v(25, 32.98) * mm, "end": v(50, 32.98) * mm, "construction": true});
            skLineSegment(sketch, "E2.direction2", {"start": v(25, 32.98) * mm, "end": v(25, 57.98) * mm, "construction": true});
            skSolve(sketch);
        }
        {
            var Q0;
            Q0=qSketchRegion(id+"F2",true);
            extrude(context, id + "F3", {"entities" : qUnion([Q0]), "operationType" : NewBodyOperationType.REMOVE, "oppositeDirection" : true, "depth" : 10 * mm});
        }
        {
            var Q0;
            Q0=makeQuery(id+"F1.opExtrude","CAP_FACE",FACE,{"disambiguationData":[OSD([sQuery(id+"F0.wireOp",EDGE,"E0.bottom"),sQuery(id+"F0.wireOp",EDGE,"E0.top"),sQuery(id+"F0.wireOp",EDGE,"E0.left"),sQuery(id+"F0.wireOp",EDGE,"E0.right")])],"isStart":false});
            var sketch = newSketch(context, id + "F4", { "sketchPlane" : qUnion([Q0])});
            skLineSegment(sketch, "E3.bottom", {"start": v(600, 382.98) * mm, "end": v(650, 382.98) * mm});
            skLineSegment(sketch, "E3.top", {"start": v(600, 207.98) * mm, "end": v(650, 207.98) * mm});
            skLineSegment(sketch, "E3.left", {"start": v(600, 382.98) * mm, "end": v(600, 207.98) * mm});
            skLineSegment(sketch, "E3.right", {"start": v(650, 382.98) * mm, "end": v(650, 207.98) * mm});
            skSolve(sketch);
        }
        {
            var Q0;
            Q0 = qSketchRegion(id + "F4", true);
            extrude(context, id + "F5", {"entities" : qUnion([Q0]), "depth" : 250 * mm});
        }
        {
            var Q0;
            Q0=makeQuery(id+"F5.opExtrude","SWEPT_FACE",FACE,{"disambiguationData":[OSD([sQuery(id+"F4.wireOp",EDGE,"E3.left")])]});
            var sketch = newSketch(context, id + "F6", { "sketchPlane" : qUnion([Q0])});
            skCircle(sketch, "E4", {"center": v(-295.48, 225) * mm, "radius": 20 * mm, "construction": true});
            skPoint(sketch, "E5", {"position": v(-295.48, 275) * mm});
            skCircle(sketch, "E6", {"center": v(-295.48, 225) * mm, "radius": 15 * mm, "construction": true});
            skCircle(sketch, "E7", {"center": v(-295.48, 240) * mm, "radius": 1.75 * mm});
            skLineSegment(sketch, "E8", {"start": v(-295.48, 225) * mm, "end": v(-295.48, 275) * mm, "construction": true});
            skCircle(sketch, "E9", {"center": v(-282.49, 217.5) * mm, "radius": 1.75 * mm});
            skCircle(sketch, "E10", {"center": v(-308.47, 217.5) * mm, "radius": 1.75 * mm});
            skLineSegment(sketch, "E11", {"start": v(-282.49, 217.5) * mm, "end": v(-295.48, 225) * mm, "construction": true});
            skLineSegment(sketch, "E12", {"start": v(-295.48, 225) * mm, "end": v(-308.47, 217.5) * mm, "construction": true});
            skSolve(sketch);
        }
        {
            var Q0;
            Q0 = qSketchRegion(id + "F6", true);
            extrude(context, id + "F7", {"entities" : qUnion([Q0]), "operationType" : NewBodyOperationType.REMOVE, "endBound" : BoundingType.THROUGH_ALL, "oppositeDirection" : true, "depth" : 25 * mm});
        }
        {
            var Q0;
            Q0=makeQuery(id+"F5.opExtrude","SWEPT_FACE",FACE,{"disambiguationData":[OSD([sQuery(id+"F4.wireOp",EDGE,"E3.left")])]});
            var sketch = newSketch(context, id + "F8", { "sketchPlane" : qUnion([Q0])});
            skCircle(sketch, "E13", {"center": v(-295.48, 225) * mm, "radius": 20 * mm});
            skPoint(sketch, "E14", {"position": v(-295.48, 275) * mm});
            skSolve(sketch);
        }
        {
            var Q0;
            Q0 = qSketchRegion(id + "F8", true);
            extrude(context, id + "F9", {"entities" : qUnion([Q0]), "depth" : 20 * mm});
        }
    });
